FREECAD ASSEMBLY — COMPONENT RECIPES ("roommake")

This assembly document has 24 components, labeled P0..P23 below (a component is one placed body or linked part). 22 of them carry a construction recipe — the FreeCAD feature program that regenerates the part from scratch, quoted from this document or its linked companion documents; the rest are supplied as boundary geometry only. No exploded tour is included for this assembly.
NOTE — this tour is split across 3 documents so each fits a 32k-token context. This is document 1: the component sections continue in the remaining 2 documents, each repeating the header above.
COMPONENT P0 — recipe-attached ("balanceball", a linked part whose construction recipe lives in a companion FreeCAD document of the same project; that document's serialized recipe follows).
Construction recipe (the companion document, serialized — sketch geometry with constraints, then the solid features built on it; lengths are millimeters unless a unit is written):

FCSTD DOCUMENT  (FreeCAD 1.0R39109 (Git))
Label: balanceball
License: All rights reserved
LicenseURL: https://en.wikipedia.org/wiki/All_rights_reserved
objects: Sketcher::SketchObject×4, PartDesign::Body×3, PartDesign::AdditiveSphere×2, PartDesign::Plane×2, App::Part×2, PartDesign::Pad×1, Part::MultiCommon×1, PartDesign::ShapeBinder×1, PartDesign::AdditivePipe×1, Part::MultiFuse×1, Part::FeaturePython×1
note: 29 computed .brp shape members not serialized (recipe doc carries the construction recipe); baked Part::Feature solids carry a one-line shape summary decoded from their .brp

FEATURE [PartDesign::AdditiveSphere] Sphere
  Angle1 = -90
  Angle2 = 90
  Angle3 = 360
  AttacherType = Attacher::AttachEngine3D
  Radius = 275
  Refine = true
  Suppressed = false
FEATURE [Sketcher::SketchObject] Sketch
  ArcFitTolerance = 1e-06
  AttachmentSupport = -> [XZ_Plane]
  ExternalGeometry = -> [Sphere]
  FullyConstrained = false
  MakeInternals = false
  MapMode = 5
  Placement = pos=(0,0,0) rot=(1,0,0;1.5708rad)
  sketch-geometry (131):
    g0: LineSegment StartX=-291.447 StartY=9.66667 StartZ=0 EndX=-291.447 EndY=10.6667 EndZ=0
    g1: LineSegment StartX=-291.447 StartY=10.6667 StartZ=0 EndX=291.447 EndY=10.6667 EndZ=0
    g2: LineSegment StartX=291.447 StartY=10.6667 StartZ=0 EndX=291.447 EndY=9.66667 EndZ=0
    g3: LineSegment StartX=291.447 StartY=9.66667 StartZ=0 EndX=-291.447 EndY=9.66667 EndZ=0
    g4: LineSegment StartX=-280.491 StartY=30 StartZ=0 EndX=-280.491 EndY=31 EndZ=0
    g5: LineSegment StartX=-280.491 StartY=31 StartZ=0 EndX=280.491 EndY=31 EndZ=0
    g6: LineSegment StartX=280.491 StartY=31 StartZ=0 EndX=280.491 EndY=30 EndZ=0
    g7: LineSegment StartX=280.491 StartY=30 StartZ=0 EndX=-280.491 EndY=30 EndZ=0
    g8: LineSegment StartX=282.77 StartY=51.3333 StartZ=0 EndX=282.77 EndY=50.3333 EndZ=0
    g9: LineSegment StartX=282.77 StartY=50.3333 StartZ=0 EndX=-282.77 EndY=50.3333 EndZ=0
    g10: LineSegment StartX=-282.77 StartY=50.3333 StartZ=0 EndX=-282.77 EndY=51.3333 EndZ=0
    g11: LineSegment StartX=-282.77 StartY=51.3333 StartZ=0 EndX=282.77 EndY=51.3333 EndZ=0
    g12: LineSegment StartX=-276.996 StartY=70.6667 StartZ=0 EndX=-276.996 EndY=71.6667 EndZ=0
    g13: LineSegment StartX=-276.996 StartY=71.6667 StartZ=0 EndX=276.996 EndY=71.6667 EndZ=0
    g14: LineSegment StartX=276.996 StartY=71.6667 StartZ=0 EndX=276.996 EndY=70.6667 EndZ=0
    g15: LineSegment StartX=276.996 StartY=70.6667 StartZ=0 EndX=-276.996 EndY=70.6667 EndZ=0
    g16: LineSegment StartX=271.883 StartY=91 StartZ=0 EndX=-271.883 EndY=91 EndZ=0
    g17: LineSegment StartX=-271.883 StartY=91 StartZ=0 EndX=-271.883 EndY=92 EndZ=0
    g18: LineSegment StartX=-271.883 StartY=92 StartZ=0 EndX=271.883 EndY=92 EndZ=0
    g19: LineSegment StartX=271.883 StartY=92 StartZ=0 EndX=271.883 EndY=91 EndZ=0
    g20: LineSegment StartX=-264.412 StartY=112.333 StartZ=0 EndX=264.412 EndY=112.333 EndZ=0
    g21: LineSegment StartX=264.412 StartY=112.333 StartZ=0 EndX=264.412 EndY=111.333 EndZ=0
    g22: LineSegment StartX=264.412 StartY=111.333 StartZ=0 EndX=-264.412 EndY=111.333 EndZ=0
    g23: LineSegment StartX=-264.412 StartY=111.333 StartZ=0 EndX=-264.412 EndY=112.333 EndZ=0
    g24: LineSegment StartX=256.154 StartY=132.667 StartZ=0 EndX=256.154 EndY=131.667 EndZ=0
    g25: LineSegment StartX=256.154 StartY=131.667 StartZ=0 EndX=-256.154 EndY=131.667 EndZ=0
    g26: LineSegment StartX=-256.154 StartY=131.667 StartZ=0 EndX=-256.154 EndY=132.667 EndZ=0
    g27: LineSegment StartX=-256.154 StartY=132.667 StartZ=0 EndX=256.154 EndY=132.667 EndZ=0
    g28: LineSegment StartX=-246.008 StartY=153 StartZ=0 EndX=246.008 EndY=153 EndZ=0
    g29: LineSegment StartX=246.008 StartY=153 StartZ=0 EndX=246.008 EndY=152 EndZ=0
    g30: LineSegment StartX=246.008 StartY=152 StartZ=0 EndX=-246.008 EndY=152 EndZ=0
    g31: LineSegment StartX=-246.008 StartY=152 StartZ=0 EndX=-246.008 EndY=153 EndZ=0
    g32: LineSegment StartX=237.302 StartY=173.333 StartZ=0 EndX=237.302 EndY=172.333 EndZ=0
    g33: LineSegment StartX=237.302 StartY=172.333 StartZ=0 EndX=-237.302 EndY=172.333 EndZ=0
    g34: LineSegment StartX=-237.302 StartY=172.333 StartZ=0 EndX=-237.302 EndY=173.333 EndZ=0
    g35: LineSegment StartX=-237.302 StartY=173.333 StartZ=0 EndX=237.302 EndY=173.333 EndZ=0
    g36: LineSegment StartX=-221.839 StartY=192.667 StartZ=0 EndX=-221.839 EndY=193.667 EndZ=0
    g37: LineSegment StartX=-221.839 StartY=193.667 StartZ=0 EndX=221.839 EndY=193.667 EndZ=0
    g38: LineSegment StartX=221.839 StartY=193.667 StartZ=0 EndX=221.839 EndY=192.667 EndZ=0
    g39: LineSegment StartX=221.839 StartY=192.667 StartZ=0 EndX=-221.839 EndY=192.667 EndZ=0
    g40: LineSegment StartX=212.405 StartY=214 StartZ=0 EndX=212.405 EndY=213 EndZ=0
    g41: LineSegment StartX=212.405 StartY=213 StartZ=0 EndX=-212.405 EndY=213 EndZ=0
    g42: LineSegment StartX=-212.405 StartY=213 StartZ=0 EndX=-212.405 EndY=214 EndZ=0
    g43: LineSegment StartX=-212.405 StartY=214 StartZ=0 EndX=212.405 EndY=214 EndZ=0
    g44: LineSegment StartX=-195.863 StartY=234.333 StartZ=0 EndX=195.863 EndY=234.333 EndZ=0
    g45: LineSegment StartX=195.863 StartY=234.333 StartZ=0 EndX=195.863 EndY=233.333 EndZ=0
    g46: LineSegment StartX=195.863 StartY=233.333 StartZ=0 EndX=-195.863 EndY=233.333 EndZ=0
    g47: LineSegment StartX=-195.863 StartY=233.333 StartZ=0 EndX=-195.863 EndY=234.333 EndZ=0
    g48: LineSegment StartX=184.098 StartY=254.667 StartZ=0 EndX=184.098 EndY=253.667 EndZ=0
    g49: LineSegment StartX=184.098 StartY=253.667 StartZ=0 EndX=-184.098 EndY=253.667 EndZ=0
    g50: LineSegment StartX=-184.098 StartY=253.667 StartZ=0 EndX=-184.098 EndY=254.667 EndZ=0
    g51: LineSegment StartX=-184.098 StartY=254.667 StartZ=0 EndX=184.098 EndY=254.667 EndZ=0
    g52: LineSegment StartX=-283.15 StartY=-10.6667 StartZ=0 EndX=-283.15 EndY=-9.66667 EndZ=0
    g53: LineSegment StartX=-283.15 StartY=-9.66667 StartZ=0 EndX=283.15 EndY=-9.66667 EndZ=0
    g54: LineSegment StartX=283.15 StartY=-9.66667 StartZ=0 EndX=283.15 EndY=-10.6667 EndZ=0
    g55: LineSegment StartX=283.15 StartY=-10.6667 StartZ=0 EndX=-283.15 EndY=-10.6667 EndZ=0
    g56: LineSegment StartX=285.733 StartY=-31 StartZ=0 EndX=-285.733 EndY=-31 EndZ=0
    g57: LineSegment StartX=-285.733 StartY=-31 StartZ=0 EndX=-285.733 EndY=-30 EndZ=0
    g58: LineSegment StartX=-285.733 StartY=-30 StartZ=0 EndX=285.733 EndY=-30 EndZ=0
    g59: LineSegment StartX=285.733 StartY=-30 StartZ=0 EndX=285.733 EndY=-31 EndZ=0
    g60: LineSegment StartX=-283.692 StartY=-51.3333 StartZ=0 EndX=-283.692 EndY=-50.3333 EndZ=0
    g61: LineSegment StartX=-283.692 StartY=-50.3333 StartZ=0 EndX=283.692 EndY=-50.3333 EndZ=0
    g62: LineSegment StartX=283.692 StartY=-50.3333 StartZ=0 EndX=283.692 EndY=-51.3333 EndZ=0
    g63: LineSegment StartX=283.692 StartY=-51.3333 StartZ=0 EndX=-283.692 EndY=-51.3333 EndZ=0
    g64: LineSegment StartX=278.903 StartY=-71.6667 StartZ=0 EndX=-278.903 EndY=-71.6667 EndZ=0
    g65: LineSegment StartX=-278.903 StartY=-71.6667 StartZ=0 EndX=-278.903 EndY=-70.6667 EndZ=0
    g66: LineSegment StartX=-278.903 StartY=-70.6667 StartZ=0 EndX=278.903 EndY=-70.6667 EndZ=0
    g67: LineSegment StartX=278.903 StartY=-70.6667 StartZ=0 EndX=278.903 EndY=-71.6667 EndZ=0
    g68: LineSegment StartX=-269.142 StartY=-92 StartZ=0 EndX=-269.142 EndY=-91 EndZ=0
    g69: LineSegment StartX=-269.142 StartY=-91 StartZ=0 EndX=269.142 EndY=-91 EndZ=0
    g70: LineSegment StartX=269.142 StartY=-91 StartZ=0 EndX=269.142 EndY=-92 EndZ=0
    g71: LineSegment StartX=269.142 StartY=-92 StartZ=0 EndX=-269.142 EndY=-92 EndZ=0
    g72: LineSegment StartX=260.857 StartY=-112.333 StartZ=0 EndX=-260.857 EndY=-112.333 EndZ=0
    g73: LineSegment StartX=-260.857 StartY=-112.333 StartZ=0 EndX=-260.857 EndY=-111.333 EndZ=0
    g74: LineSegment StartX=-260.857 StartY=-111.333 StartZ=0 EndX=260.857 EndY=-111.333 EndZ=0
    g75: LineSegment StartX=260.857 StartY=-111.333 StartZ=0 EndX=260.857 EndY=-112.333 EndZ=0
    g76: LineSegment StartX=-246.128 StartY=-132.667 StartZ=0 EndX=-246.128 EndY=-131.667 EndZ=0
    g77: LineSegment StartX=-246.128 StartY=-131.667 StartZ=0 EndX=246.128 EndY=-131.667 EndZ=0
    g78: LineSegment StartX=246.128 StartY=-131.667 StartZ=0 EndX=246.128 EndY=-132.667 EndZ=0
    g79: LineSegment StartX=246.128 StartY=-132.667 StartZ=0 EndX=-246.128 EndY=-132.667 EndZ=0
    g80: LineSegment StartX=237.57 StartY=-153 StartZ=0 EndX=-237.57 EndY=-153 EndZ=0
    g81: LineSegment StartX=-237.57 StartY=-153 StartZ=0 EndX=-237.57 EndY=-152 EndZ=0
    g82: LineSegment StartX=-237.57 StartY=-152 StartZ=0 EndX=237.57 EndY=-152 EndZ=0
    g83: LineSegment StartX=237.57 StartY=-152 StartZ=0 EndX=237.57 EndY=-153 EndZ=0
    g84: LineSegment StartX=-225.124 StartY=-173.333 StartZ=0 EndX=-225.124 EndY=-172.333 EndZ=0
    g85: LineSegment StartX=-225.124 StartY=-172.333 StartZ=0 EndX=225.124 EndY=-172.333 EndZ=0
    g86: LineSegment StartX=225.124 StartY=-172.333 StartZ=0 EndX=225.124 EndY=-173.333 EndZ=0
    g87: LineSegment StartX=225.124 StartY=-173.333 StartZ=0 EndX=-225.124 EndY=-173.333 EndZ=0
    g88: LineSegment StartX=209.157 StartY=-193.667 StartZ=0 EndX=-209.157 EndY=-193.667 EndZ=0
    g89: LineSegment StartX=-209.157 StartY=-193.667 StartZ=0 EndX=-209.157 EndY=-192.667 EndZ=0
    g90: LineSegment StartX=-209.157 StartY=-192.667 StartZ=0 EndX=209.157 EndY=-192.667 EndZ=0
    g91: LineSegment StartX=209.157 StartY=-192.667 StartZ=0 EndX=209.157 EndY=-193.667 EndZ=0
    g92: LineSegment StartX=-190.627 StartY=-214 StartZ=0 EndX=-190.627 EndY=-213 EndZ=0
    g93: LineSegment StartX=-190.627 StartY=-213 StartZ=0 EndX=190.627 EndY=-213 EndZ=0
    g94: LineSegment StartX=190.627 StartY=-213 StartZ=0 EndX=190.627 EndY=-214 EndZ=0
    g95: LineSegment StartX=190.627 StartY=-214 StartZ=0 EndX=-190.627 EndY=-214 EndZ=0
    g96: LineSegment StartX=-172.023 StartY=-234.333 StartZ=0 EndX=-172.023 EndY=-233.333 EndZ=0
    g97: LineSegment StartX=-172.023 StartY=-233.333 StartZ=0 EndX=172.023 EndY=-233.333 EndZ=0
    g98: LineSegment StartX=172.023 StartY=-233.333 StartZ=0 EndX=172.023 EndY=-234.333 EndZ=0
    g99: LineSegment StartX=172.023 StartY=-234.333 StartZ=0 EndX=-172.023 EndY=-234.333 EndZ=0
    g100: LineSegment StartX=-150.671 StartY=-254.667 StartZ=0 EndX=-150.671 EndY=-253.667 EndZ=0
    g101: LineSegment StartX=-150.671 StartY=-253.667 StartZ=0 EndX=150.671 EndY=-253.667 EndZ=0
    g102: LineSegment StartX=150.671 StartY=-253.667 StartZ=0 EndX=150.671 EndY=-254.667 EndZ=0
    g103: LineSegment StartX=150.671 StartY=-254.667 StartZ=0 EndX=-150.671 EndY=-254.667 EndZ=0
    g104: LineSegment [constr] StartX=8.42e-14 StartY=275 StartZ=0 EndX=8.42e-14 EndY=253.667 EndZ=0
    g105: LineSegment [constr] StartX=7.37e-14 StartY=254.667 StartZ=0 EndX=7.37e-14 EndY=233.333 EndZ=0
    g106: LineSegment [constr] StartX=6.83e-14 StartY=234.333 StartZ=0 EndX=6.83e-14 EndY=213 EndZ=0
    g107: LineSegment [constr] StartX=9.01e-14 StartY=214 StartZ=0 EndX=9.01e-14 EndY=192.667 EndZ=0
    g108: LineSegment [constr] StartX=7.41e-14 StartY=193.667 StartZ=0 EndX=7.41e-14 EndY=172.333 EndZ=0
    g109: LineSegment [constr] StartX=8.64e-14 StartY=173.333 StartZ=0 EndX=8.64e-14 EndY=152 EndZ=0
    g110: LineSegment [constr] StartX=8.72e-14 StartY=153 StartZ=0 EndX=8.72e-14 EndY=131.667 EndZ=0
    g111: LineSegment [constr] StartX=1.192e-13 StartY=132.667 StartZ=0 EndX=1.192e-13 EndY=111.333 EndZ=0
    g112: LineSegment [constr] StartX=1.25e-13 StartY=112.333 StartZ=0 EndX=1.25e-13 EndY=91 EndZ=0
    g113: LineSegment [constr] StartX=1.363e-13 StartY=92 StartZ=0 EndX=1.363e-13 EndY=70.6667 EndZ=0
    g114: LineSegment [constr] StartX=1.131e-13 StartY=71.6667 StartZ=0 EndX=1.131e-13 EndY=50.3333 EndZ=0
    g115: LineSegment [constr] StartX=8.7e-14 StartY=51.3333 StartZ=0 EndX=8.7e-14 EndY=30 EndZ=0
    g116: LineSegment [constr] StartX=1.326e-13 StartY=31 StartZ=0 EndX=1.326e-13 EndY=9.66667 EndZ=0
    g117: LineSegment [constr] StartX=9.7e-14 StartY=10.6667 StartZ=0 EndX=9.7e-14 EndY=-10.6667 EndZ=0
    g118: LineSegment [constr] StartX=1.219e-13 StartY=-9.66667 StartZ=0 EndX=1.219e-13 EndY=-31 EndZ=0
    g119: LineSegment [constr] StartX=8.3e-14 StartY=-30 StartZ=0 EndX=8.3e-14 EndY=-51.3333 EndZ=0
    g120: LineSegment [constr] StartX=9.47e-14 StartY=-50.3333 StartZ=0 EndX=9.47e-14 EndY=-71.6667 EndZ=0
    g121: LineSegment [constr] StartX=1.138e-13 StartY=-70.6667 StartZ=0 EndX=1.138e-13 EndY=-92 EndZ=0
    g122: LineSegment [constr] StartX=1.058e-13 StartY=-91 StartZ=0 EndX=1.058e-13 EndY=-112.333 EndZ=0
    g123: LineSegment [constr] StartX=1.327e-13 StartY=-111.333 StartZ=0 EndX=1.327e-13 EndY=-132.667 EndZ=0
    g124: LineSegment [constr] StartX=1.275e-13 StartY=-131.667 StartZ=0 EndX=1.275e-13 EndY=-153 EndZ=0
    g125: LineSegment [constr] StartX=1.325e-13 StartY=-152 StartZ=0 EndX=1.325e-13 EndY=-173.333 EndZ=0
    g126: LineSegment [constr] StartX=1.362e-13 StartY=-172.333 StartZ=0 EndX=1.362e-13 EndY=-193.667 EndZ=0
    g127: LineSegment [constr] StartX=1.246e-13 StartY=-192.667 StartZ=0 EndX=1.246e-13 EndY=-214 EndZ=0
    g128: LineSegment [constr] StartX=1.449e-13 StartY=-213 StartZ=0 EndX=1.449e-13 EndY=-234.333 EndZ=0
    g129: LineSegment [constr] StartX=1.405e-13 StartY=-233.333 StartZ=0 EndX=1.405e-13 EndY=-254.667 EndZ=0
    g130: LineSegment [constr] StartX=1.48e-13 StartY=-253.667 StartZ=0 EndX=-5.05e-14 EndY=-275 EndZ=0
  constraints (340):
    c: Coincident(g0,g1)
    c: Coincident(g1,g2)
    c: Coincident(g2,g3)
    c: Coincident(g3,g0)
    c: Vertical(g0)
    c: Vertical(g2)
    c: Horizontal(g1)
    c: Horizontal(g3)
    c: Coincident(g4,g5)
    c: Coincident(g5,g6)
    c: Coincident(g6,g7)
    c: Coincident(g7,g4)
    c: Vertical(g4)
    c: Vertical(g6)
    c: Horizontal(g5)
    c: Horizontal(g7)
    c: Coincident(g8,g9)
    c: Coincident(g9,g10)
    c: Coincident(g10,g11)
    c: Coincident(g11,g8)
    c: Vertical(g8)
    c: Vertical(g10)
    c: Horizontal(g9)
    c: Horizontal(g11)
    c: Coincident(g12,g13)
    c: Coincident(g13,g14)
    c: Coincident(g14,g15)
    c: Coincident(g15,g12)
    c: Vertical(g12)
    c: Vertical(g14)
    c: Horizontal(g13)
    c: Horizontal(g15)
    c: Coincident(g16,g17)
    c: Coincident(g17,g18)
    c: Coincident(g18,g19)
    c: Coincident(g19,g16)
    c: Horizontal(g16)
    c: Horizontal(g18)
    c: Vertical(g17)
    c: Vertical(g19)
    c: Coincident(g20,g21)
    c: Coincident(g21,g22)
    c: Coincident(g22,g23)
    c: Coincident(g23,g20)
    c: Horizontal(g20)
    c: Horizontal(g22)
    c: Vertical(g21)
    c: Vertical(g23)
    c: Coincident(g24,g25)
    c: Coincident(g25,g26)
    c: Coincident(g26,g27)
    c: Coincident(g27,g24)
    c: Vertical(g24)
    c: Vertical(g26)
    c: Horizontal(g25)
    c: Horizontal(g27)
    c: Coincident(g28,g29)
    c: Coincident(g29,g30)
    c: Coincident(g30,g31)
    c: Coincident(g31,g28)
    c: Horizontal(g28)
    c: Horizontal(g30)
    c: Vertical(g29)
    c: Vertical(g31)
    c: Coincident(g32,g33)
    c: Coincident(g33,g34)
    c: Coincident(g34,g35)
    c: Coincident(g35,g32)
    c: Vertical(g32)
    c: Vertical(g34)
    c: Horizontal(g33)
    c: Horizontal(g35)
    c: Coincident(g36,g37)
    c: Coincident(g37,g38)
    c: Coincident(g38,g39)
    c: Coincident(g39,g36)
    c: Vertical(g36)
    c: Vertical(g38)
    c: Horizontal(g37)
    c: Horizontal(g39)
    c: Coincident(g40,g41)
    c: Coincident(g41,g42)
    c: Coincident(g42,g43)
    c: Coincident(g43,g40)
    c: Vertical(g40)
    c: Vertical(g42)
    c: Horizontal(g41)
    c: Horizontal(g43)
    c: Coincident(g44,g45)
    c: Coincident(g45,g46)
    c: Coincident(g46,g47)
    c: Coincident(g47,g44)
    c: Horizontal(g44)
    c: Horizontal(g46)
    c: Vertical(g45)
    c: Vertical(g47)
    c: Coincident(g48,g49)
    c: Coincident(g49,g50)
    c: Coincident(g50,g51)
    c: Coincident(g51,g48)
    c: Vertical(g48)
    c: Vertical(g50)
    c: Horizontal(g49)
    c: Horizontal(g51)
    c: Coincident(g52,g53)
    c: Coincident(g53,g54)
    c: Coincident(g54,g55)
    c: Coincident(g55,g52)
    c: Vertical(g52)
    c: Vertical(g54)
    c: Horizontal(g53)
    c: Horizontal(g55)
    c: Coincident(g56,g57)
    c: Coincident(g57,g58)
    c: Coincident(g58,g59)
    c: Coincident(g59,g56)
    c: Horizontal(g56)
    c: Horizontal(g58)
    c: Vertical(g57)
    c: Vertical(g59)
    c: Coincident(g60,g61)
    c: Coincident(g61,g62)
    c: Coincident(g62,g63)
    c: Coincident(g63,g60)
    c: Vertical(g60)
    c: Vertical(g62)
    c: Horizontal(g61)
    c: Horizontal(g63)
    c: Coincident(g64,g65)
    c: Coincident(g65,g66)
    c: Coincident(g66,g67)
    c: Coincident(g67,g64)
    c: Horizontal(g64)
    c: Horizontal(g66)
    c: Vertical(g65)
    c: Vertical(g67)
    c: Coincident(g68,g69)
    c: Coincident(g69,g70)
    c: Coincident(g70,g71)
    c: Coincident(g71,g68)
    c: Vertical(g68)
    c: Vertical(g70)
    c: Horizontal(g69)
    c: Horizontal(g71)
    c: Coincident(g72,g73)
    c: Coincident(g73,g74)
    c: Coincident(g74,g75)
    c: Coincident(g75,g72)
    c: Horizontal(g72)
    c: Horizontal(g74)
    c: Vertical(g73)
    c: Vertical(g75)
    c: Coincident(g76,g77)
    c: Coincident(g77,g78)
    c: Coincident(g78,g79)
    c: Coincident(g79,g76)
    c: Vertical(g76)
    c: Vertical(g78)
    c: Horizontal(g77)
    c: Horizontal(g79)
    c: Coincident(g80,g81)
    c: Coincident(g81,g82)
    c: Coincident(g82,g83)
    c: Coincident(g83,g80)
    c: Horizontal(g80)
    c: Horizontal(g82)
    c: Vertical(g81)
    c: Vertical(g83)
    c: Coincident(g84,g85)
    c: Coincident(g85,g86)
    c: Coincident(g86,g87)
    c: Coincident(g87,g84)
    c: Vertical(g84)
    c: Vertical(g86)
    c: Horizontal(g85)
    c: Horizontal(g87)
    c: Coincident(g88,g89)
    c: Coincident(g89,g90)
    c: Coincident(g90,g91)
    c: Coincident(g91,g88)
    c: Horizontal(g88)
    c: Horizontal(g90)
    c: Vertical(g89)
    c: Vertical(g91)
    c: Coincident(g92,g93)
    c: Coincident(g93,g94)
    c: Coincident(g94,g95)
    c: Coincident(g95,g92)
    c: Vertical(g92)
    c: Vertical(g94)
    c: Horizontal(g93)
    c: Horizontal(g95)
    c: Coincident(g96,g97)
    c: Coincident(g97,g98)
    c: Coincident(g98,g99)
    c: Coincident(g99,g96)
    c: Vertical(g96)
    c: Vertical(g98)
    c: Horizontal(g97)
    c: Horizontal(g99)
    c: Coincident(g100,g101)
    c: Coincident(g101,g102)
    c: Coincident(g102,g103)
    c: Coincident(g103,g100)
    c: Vertical(g100)
    c: Vertical(g102)
    c: Horizontal(g101)
    c: Horizontal(g103)
    c: Equal(g50,g47)
    c: Equal(g47,g42)
    c: Equal(g42,g36)
    c: Equal(g36,g34)
    c: Equal(g34,g31)
    c: Equal(g31,g26)
    c: Equal(g26,g23)
    c: Equal(g23,g17)
    c: Equal(g17,g12)
    c: Equal(g12,g10)
    c: Equal(g10,g4)
    c: Equal(g4,g0)
    c: Equal(g0,g52)
    c: Equal(g52,g57)
    c: Equal(g57,g60)
    c: Equal(g60,g65)
    c: Equal(g65,g68)
    c: Equal(g68,g73)
    c: Equal(g73,g76)
    c: Equal(g76,g81)
    c: Equal(g81,g84)
    c: Equal(g84,g89)
    c: Equal(g89,g92)
    c: Equal(g92,g96)
    c: Equal(g96,g100)
    c: Coincident(g104,g-3)
    c: Symmetric(g49,g49,g104)
    c: Symmetric(g51,g51,g105)
    c: Symmetric(g46,g46,g105)
    c: Symmetric(g44,g44,g106)
    c: Symmetric(g41,g41,g106)
    c: Symmetric(g43,g43,g107)
    c: Symmetric(g39,g39,g107)
    c: Symmetric(g37,g37,g108)
    c: Symmetric(g33,g33,g108)
    c: Vertical(g108)
    c: Symmetric(g35,g35,g109)
    c: Symmetric(g30,g30,g109)
    c: Symmetric(g28,g28,g110)
    c: Symmetric(g25,g25,g110)
    c: Symmetric(g27,g27,g111)
    c: Symmetric(g22,g22,g111)
    c: Vertical(g111)
    c: Symmetric(g20,g20,g112)
    c: Symmetric(g16,g16,g112)
    c: Vertical(g112)
    c: Symmetric(g18,g18,g113)
    c: Symmetric(g15,g15,g113)
    c: Symmetric(g13,g13,g114)
    c: Symmetric(g9,g9,g114)
    c: Symmetric(g11,g11,g115)
    c: Symmetric(g7,g7,g115)
    c: Vertical(g115)
    c: Symmetric(g5,g5,g116)
    c: Symmetric(g3,g3,g116)
    c: Symmetric(g1,g1,g117)
    c: Symmetric(g55,g55,g117)
    c: Symmetric(g53,g53,g118)
    c: Symmetric(g56,g56,g118)
    c: Symmetric(g58,g58,g119)
    c: Symmetric(g63,g63,g119)
    c: Symmetric(g61,g61,g120)
    c: Symmetric(g64,g64,g120)
    c: Symmetric(g66,g66,g121)
    c: Symmetric(g71,g71,g121)
    c: Symmetric(g69,g69,g122)
    c: Symmetric(g72,g72,g122)
    c: Vertical(g122)
    c: Symmetric(g74,g74,g123)
    c: Symmetric(g79,g79,g123)
    c: Symmetric(g77,g77,g124)
    c: Symmetric(g80,g80,g124)
    c: Symmetric(g82,g82,g125)
    c: Symmetric(g87,g87,g125)
    c: Symmetric(g85,g85,g126)
    c: Symmetric(g88,g88,g126)
    c: Symmetric(g90,g90,g127)
    c: Symmetric(g95,g95,g127)
    c: Symmetric(g93,g93,g128)
    c: Symmetric(g99,g99,g128)
    c: Symmetric(g97,g97,g129)
    c: Symmetric(g103,g103,g129)
    c: Symmetric(g101,g101,g130)
    c: Coincident(g130,g-3)
    c: Equal(g104,g105)
    c: Equal(g105,g106)
    c: Equal(g106,g107)
    c: Equal(g107,g108)
    c: Equal(g108,g109)
    c: Equal(g109,g110)
    c: Equal(g110,g111)
    c: Equal(g111,g112)
    c: Equal(g112,g113)
    c: Equal(g113,g114)
    c: Equal(g114,g115)
    c: Equal(g115,g116)
    c: Equal(g116,g117)
    c: Equal(g117,g118)
    c: Equal(g118,g119)
    c: Equal(g119,g120)
    c: Equal(g120,g121)
    c: Equal(g121,g122)
    c: Equal(g122,g123)
    c: Equal(g123,g124)
    c: Equal(g124,g125)
    c: Equal(g125,g126)
    c: Equal(g126,g127)
    c: Equal(g127,g128)
    c: Equal(g128,g129)
    c: Equal(g129,g130)
    c: Vertical(g104)
    c: Vertical(g105)
    c: Vertical(g106)
    c: Vertical(g107)
    c: Vertical(g109)
    c: Vertical(g110)
    c: Vertical(g113)
    c: Vertical(g114)
    c: Vertical(g116)
    c: Vertical(g117)
    c: Vertical(g118)
    c: Vertical(g119)
    c: Vertical(g120)
    c: Vertical(g121)
    c: Vertical(g123)
    c: Vertical(g124)
    c: Vertical(g125)
    c: Vertical(g126)
    c: Vertical(g127)
    c: Vertical(g128)
    c: Vertical(g129)
    c: DistanceY(g50,g50) = 1
FEATURE [PartDesign::Pad] Pad
  BaseFeature = -> Sphere
  Direction = (0,-1,2e-16)
  Length = 560
  Length2 = 10
  Midplane = true
  Profile = -> Sketch
  ReferenceAxis = -> Sketch [N_Axis]
  Refine = true
  Suppressed = false
  Type = 0
FEATURE [PartDesign::Body] Body
  AllowCompound = false
  Group = -> [Sphere,Sketch,Pad]
  Origin = -> Origin
  Tip = -> Pad
FEATURE [PartDesign::AdditiveSphere] Sphere001
  Angle1 = -90
  Angle2 = 90
  Angle3 = 360
  AttacherType = Attacher::AttachEngine3D
  Radius = 275.5
  Refine = true
  Suppressed = false
FEATURE [PartDesign::Body] Body001
  AllowCompound = false
  Group = -> [Sphere001]
  Origin = -> Origin001
  Tip = -> Sphere001
FEATURE [Part::MultiCommon] Common
  Refine = true
  Shapes = -> [Body,Body001]
FEATURE [PartDesign::ShapeBinder] CopyCommon
  TraceSupport = false
FEATURE [Sketcher::SketchObject] Sketch001
  ArcFitTolerance = 1e-06
  AttachmentSupport = -> [XZ_Plane002]
  ExternalGeometry = -> [CopyCommon]
  FullyConstrained = false
  MakeInternals = false
  MapMode = 5
  Placement = pos=(0,0,0) rot=(1,0,0;1.5708rad)
  sketch-geometry (2):
    g0: Circle CenterX=-157.732 CenterY=-255.772 CenterZ=0 NormalX=0 NormalY=0 NormalZ=1 AngleXU=0 Radius=25
    g1: LineSegment StartX=-144.873 StartY=-234.333 StartZ=0 EndX=-157.732 EndY=-255.772 EndZ=0
  constraints (4):
    c: PointOnObject(g-3,g0)
    c: Radius(g0) = 25
    c: Coincident(g1,g-3)
    c: Coincident(g1,g0)
FEATURE [PartDesign::Plane] DatumPlane
  AttachmentSupport = -> [Sketch001]
  Length = 438.471
  MapMode = 1
  Placement = pos=(-157.732,-5.68e-14,-255.772) rot=(0,0,1;0rad)
  ResizeMode = 0
  Width = 438.506
FEATURE [Sketcher::SketchObject] Sketch002
  ArcFitTolerance = 1e-06
  AttachmentSupport = -> [DatumPlane]
  ExternalGeometry = -> [CopyCommon]
  FullyConstrained = true
  MakeInternals = false
  MapMode = 5
  Placement = pos=(-157.732,-5.68e-14,-255.772) rot=(0,0,1;0rad)
  sketch-geometry (1):
    g0: Circle CenterX=157.732 CenterY=4.8e-15 CenterZ=0 NormalX=0 NormalY=0 NormalZ=1 AngleXU=0 Radius=157.732
  constraints (2):
    c: Coincident(g0,g-3)
    c: PointOnObject(g-1,g0)
FEATURE [PartDesign::Plane] DatumPlane001
  AttachmentSupport = -> [Sketch001]
  Length = 372.613
  MapMode = 11
  Placement = pos=(-157.732,-5.68e-14,-255.772) rot=(0.57735,-0.57735,0.57735;2.0944rad)
  ResizeMode = 0
  Width = 432.239
FEATURE [Sketcher::SketchObject] Sketch003
  ArcFitTolerance = 1e-06
  AttachmentSupport = -> [DatumPlane001]
  ExternalGeometry = -> [Sketch001]
  FullyConstrained = false
  MakeInternals = false
  MapMode = 5
  Placement = pos=(-157.732,-5.68e-14,-255.772) rot=(0.57735,-0.57735,0.57735;2.0944rad)
  sketch-geometry (1):
    g0: Circle CenterX=0 CenterY=0 CenterZ=0 NormalX=0 NormalY=0 NormalZ=1 AngleXU=0 Radius=25
  constraints (1):
    c: Coincident(g0,g-1)
FEATURE [PartDesign::AdditivePipe] AdditivePipe
  AuxilleryCurvelinear = true
  AuxillerySpineTangent = false
  Binormal = (0,0,0)
  Mode = 0
  Placement = pos=(-157.732,-5.68e-14,-255.772) rot=(0.57735,-0.57735,0.57735;2.0944rad)
  Profile = -> Sketch003
  Refine = true
  Spine = -> Sketch002
  SpineTangent = false
  Suppressed = false
  Transformation = 0
  Transition = 0
FEATURE [PartDesign::Body] Body002
  AllowCompound = false
  Group = -> [CopyCommon,Sketch001,DatumPlane,Sketch002,DatumPlane001,Sketch003,AdditivePipe]
  Origin = -> Origin002
  Tip = -> AdditivePipe
FEATURE [Part::MultiFuse] Fusion
  Placement = pos=(0,0,280) rot=(0,0,1;0rad)
  Refine = true
  Shapes = -> [Common,Body002]
FEATURE [App::Part] Part  label="balanceball1"
  Group = -> [Body,Body001,Common,Body002,Fusion]
  Origin = -> Origin003
  Placement = pos=(0,0,280) rot=(0,0,1;0rad)
FEATURE [Part::FeaturePython] Clone  label="balanceball_clone"  # Draft clone (typed FeaturePython)
  AttacherType = Attacher::AttachEngine3D
  Fuse = false
  Objects = -> [Part]
  Scale = (1,1,1)
FEATURE [App::Part] Part001  label="balanceball"
  Group = -> [Clone]
  Origin = -> Origin004
COMPONENT P1 — recipe-attached ("clock", a linked part whose construction recipe lives in a companion FreeCAD document of the same project; that document's serialized recipe follows).
Construction recipe (the companion document, serialized — sketch geometry with constraints, then the solid features built on it; lengths are millimeters unless a unit is written):

FCSTD DOCUMENT  (FreeCAD 1.0R39109 (Git))
Label: clock
License: All rights reserved
LicenseURL: https://en.wikipedia.org/wiki/All_rights_reserved
objects: Part::FeaturePython×13, App::Part×13, Sketcher::SketchObject×6, PartDesign::Body×6, PartDesign::ShapeBinder×5, PartDesign::Pad×5, PartDesign::Revolution×1
note: 53 computed .brp shape members not serialized (recipe doc carries the construction recipe); baked Part::Feature solids carry a one-line shape summary decoded from their .brp

FEATURE [Sketcher::SketchObject] Sketch
  ArcFitTolerance = 1e-06
  AttachmentSupport = -> [XZ_Plane]
  FullyConstrained = true
  MakeInternals = false
  MapMode = 5
  Placement = pos=(0,0,0) rot=(1,0,0;1.5708rad)
  sketch-geometry (12):
    g0: LineSegment StartX=0 StartY=0 StartZ=0 EndX=150 EndY=0 EndZ=0
    g1: LineSegment StartX=150 StartY=0 StartZ=0 EndX=150 EndY=55 EndZ=0
    g2: LineSegment StartX=150 StartY=55 StartZ=0 EndX=135 EndY=55 EndZ=0
    g3: LineSegment StartX=135 StartY=55 StartZ=0 EndX=135 EndY=50 EndZ=0
    g4: LineSegment StartX=135 StartY=50 StartZ=0 EndX=140 EndY=50 EndZ=0
    g5: LineSegment StartX=140 StartY=50 StartZ=0 EndX=140 EndY=48 EndZ=0
    g6: LineSegment StartX=140 StartY=48 StartZ=0 EndX=135 EndY=48 EndZ=0
    g7: LineSegment StartX=135 StartY=48 StartZ=0 EndX=135 EndY=25 EndZ=0
    g8: LineSegment StartX=135 StartY=25 StartZ=0 EndX=2.5 EndY=25 EndZ=0
    g9: LineSegment StartX=2.5 StartY=25 StartZ=0 EndX=2.5 EndY=28 EndZ=0
    g10: LineSegment StartX=2.5 StartY=28 StartZ=0 EndX=0 EndY=28 EndZ=0
    g11: LineSegment StartX=0 StartY=28 StartZ=0 EndX=0 EndY=0 EndZ=0
  constraints (35):
    c: Coincident(g-1,g0)
    c: PointOnObject(g0,g-1)
    c: Coincident(g0,g1)
    c: Vertical(g1)
    c: Coincident(g1,g2)
    c: Horizontal(g2)
    c: Coincident(g2,g3)
    c: Vertical(g3)
    c: Coincident(g3,g4)
    c: Horizontal(g4)
    c: Coincident(g4,g5)
    c: Vertical(g5)
    c: Coincident(g5,g6)
    c: Horizontal(g6)
    c: Coincident(g6,g7)
    c: Vertical(g7)
    c: Coincident(g7,g8)
    c: Horizontal(g8)
    c: Coincident(g8,g9)
    c: Vertical(g9)
    c: Coincident(g9,g10)
    c: PointOnObject(g10,g-2)
    c: Horizontal(g10)
    c: Coincident(g10,g11)
    c: Coincident(g11,g0)
    c: DistanceX(g0,g0) = 150
    c: DistanceY(g1,g1) = 55
    c: DistanceX(g2,g2) = 15
    c: DistanceY(g3,g3) = 5
    c: DistanceX(g4,g4) = 5
    c: Equal(g4,g6)
    c: DistanceY(g5,g5) = 2
    c: DistanceY(g7,g2) = 30
    c: DistanceY(g9,g9) = 3
    c: DistanceX(g10,g10) = 2.5
FEATURE [PartDesign::Revolution] Revolution
  Angle = 360
  Angle2 = 60
  Axis = (0,2e-16,1)
  Base = (0,0,0)
  Placement = pos=(0,0,0) rot=(1,0,0;1.5708rad)
  Profile = -> Sketch
  ReferenceAxis = -> Sketch [V_Axis]
  Refine = true
  Reversed = true
  Suppressed = false
  Type = 0
FEATURE [PartDesign::Body] Body
  AllowCompound = false
  Group = -> [Sketch,Revolution]
  Origin = -> Origin
  Tip = -> Revolution
FEATURE [PartDesign::ShapeBinder] CopyRevolution
  Placement = pos=(0,0,0) rot=(1,0,0;1.5708rad)
  TraceSupport = false
FEATURE [Sketcher::SketchObject] Sketch001
  ArcFitTolerance = 1e-06
  AttachmentSupport = -> [CopyRevolution]
  FullyConstrained = true
  MakeInternals = false
  MapMode = 5
  Placement = pos=(0,1.1e-14,25) rot=(0,0,1;3.14159rad)
  sketch-geometry (5):
    g0: Circle CenterX=0 CenterY=6e-16 CenterZ=0 NormalX=0 NormalY=0 NormalZ=1 AngleXU=0 Radius=2.5
    g1: ArcOfCircle CenterX=0 CenterY=6e-16 CenterZ=0 NormalX=0 NormalY=0 NormalZ=1 AngleXU=0 Radius=5 StartAngle=1e-16 EndAngle=3.14159
    g2: LineSegment StartX=5 StartY=1.2e-15 StartZ=0 EndX=5 EndY=-100 EndZ=0
    g3: LineSegment StartX=5 StartY=-100 StartZ=0 EndX=-5 EndY=-100 EndZ=0
    g4: LineSegment StartX=-5 StartY=-100 StartZ=0 EndX=-5 EndY=0 EndZ=0
  constraints (13):
    c: Coincident(g1,g0)
    c: Radius(g0) = 2.5
    c: PointOnObject(g0,g-2)
    c: Vertical(g2)
    c: Coincident(g2,g3)
    c: Horizontal(g3)
    c: Coincident(g3,g4)
    c: Vertical(g4)
    c: PointOnObject(g4,g-1)
    c: Tangent(g1,g4) = 1.5708
    c: Tangent(g1,g2) = 1.5708
    c: DistanceX(g3,g3) = 10
    c: DistanceY(g4,g4) = 100
FEATURE [PartDesign::Pad] Pad
  Direction = (0,0,1)
  Length = 1
  Length2 = 10
  Placement = pos=(0,0,0) rot=(1,0,0;1.5708rad)
  Profile = -> Sketch001
  ReferenceAxis = -> Sketch001 [N_Axis]
  Refine = true
  Suppressed = false
  Type = 0
FEATURE [PartDesign::Body] Body001
  AllowCompound = false
  Group = -> [CopyRevolution,Sketch001,Pad]
  Origin = -> Origin001
  Tip = -> Pad
FEATURE [PartDesign::ShapeBinder] CopyRevolution001
  Placement = pos=(0,0,0) rot=(1,0,0;1.5708rad)
  TraceSupport = false
FEATURE [Sketcher::SketchObject] Sketch002
  ArcFitTolerance = 1e-06
  AttachmentSupport = -> [CopyRevolution001]
  FullyConstrained = true
  MakeInternals = false
  MapMode = 5
  Placement = pos=(0,1.1e-14,25) rot=(0,0,1;3.14159rad)
  sketch-geometry (5):
    g0: Circle CenterX=0 CenterY=0 CenterZ=0 NormalX=0 NormalY=0 NormalZ=1 AngleXU=0 Radius=2.5
    g1: ArcOfCircle CenterX=0 CenterY=0 CenterZ=0 NormalX=0 NormalY=0 NormalZ=1 AngleXU=0 Radius=5 StartAngle=0 EndAngle=3.14159
    g2: LineSegment StartX=5 StartY=0 StartZ=0 EndX=5 EndY=-65 EndZ=0
    g3: LineSegment StartX=5 StartY=-65 StartZ=0 EndX=-5 EndY=-65 EndZ=0
    g4: LineSegment StartX=-5 StartY=-65 StartZ=0 EndX=-5 EndY=0 EndZ=0
  constraints (12):
    c: Coincident(g1,g0)
    c: Radius(g0) = 2.5
    c: Coincident(g0,g-1)
    c: PointOnObject(g2,g-1)
    c: Coincident(g2,g3)
    c: Horizontal(g3)
    c: Coincident(g3,g4)
    c: PointOnObject(g4,g-1)
    c: Tangent(g1,g4) = 1.5708
    c: Tangent(g1,g2) = 1.5708
    c: DistanceX(g3,g3) = 10
    c: DistanceY(g4,g4) = 65
FEATURE [PartDesign::Pad] Pad001
  Direction = (0,0,1)
  Length = 1
  Length2 = 10
  Placement = pos=(0,0,0) rot=(1,0,0;1.5708rad)
  Profile = -> Sketch002
  ReferenceAxis = -> Sketch002 [N_Axis]
  Refine = true
  Suppressed = false
  Type = 0
FEATURE [PartDesign::Body] Body002
  AllowCompound = false
  Group = -> [CopyRevolution001,Sketch002,Pad001]
  Origin = -> Origin002
  Placement = pos=(0,0,1) rot=(0,0,1;1.0472rad)
  Tip = -> Pad001
FEATURE [PartDesign::ShapeBinder] CopyRevolution002
  Placement = pos=(0,0,0) rot=(1,0,0;1.5708rad)
  TraceSupport = false
FEATURE [Sketcher::SketchObject] Sketch003
  ArcFitTolerance = 1e-06
  AttachmentSupport = -> [CopyRevolution002]
  FullyConstrained = false
  MakeInternals = false
  MapMode = 5
  Placement = pos=(0,1.1e-14,25) rot=(0,0,1;3.14159rad)
  sketch-geometry (6):
    g0: Circle CenterX=0 CenterY=0 CenterZ=0 NormalX=0 NormalY=0 NormalZ=1 AngleXU=0 Radius=2.5
    g1: ArcOfCircle CenterX=0 CenterY=0 CenterZ=0 NormalX=0 NormalY=0 NormalZ=1 AngleXU=0 Radius=5 StartAngle=0.986756 EndAngle=6.86723
    g2: LineSegment StartX=4.17121 StartY=2.75699 StartZ=0 EndX=88.2635 EndY=86.8493 EndZ=0
    g3: LineSegment StartX=88.2635 StartY=86.8493 StartZ=0 EndX=86.8493 EndY=88.2635 EndZ=0
    g4: LineSegment StartX=2.75699 StartY=4.17121 StartZ=0 EndX=86.8493 EndY=88.2635 EndZ=0
    g5: LineSegment [constr] StartX=0 StartY=0 StartZ=0 EndX=87.5564 EndY=87.5564 EndZ=0
  constraints (14):
    c: Coincident(g0,g-1)
    c: Coincident(g0,g1)
    c: Radius(g0) = 2.5
    c: Coincident(g3,g2)
    c: Coincident(g4,g3)
    c: Coincident(g5,g0)
    c: Symmetric(g3,g3,g5)
    c: Angle(g-1,g5) = 0.785398
    c: Perpendicular(g3,g4)
    c: Perpendicular(g2,g3)
    c: Distance(g3) = 2
    c: Coincident(g1,g2)
    c: Coincident(g1,g4)
    c: Radius(g1) = 5
FEATURE [PartDesign::Pad] Pad002
  Direction = (0,0,1)
  Length = 0.5
  Length2 = 10
  Placement = pos=(0,0,0) rot=(1,0,0;1.5708rad)
  Profile = -> Sketch003
  ReferenceAxis = -> Sketch003 [N_Axis]
  Refine = true
  Suppressed = false
  Type = 0
FEATURE [PartDesign::Body] Body003
  AllowCompound = false
  Group = -> [CopyRevolution002,Sketch003,Pad002]
  Origin = -> Origin003
  Placement = pos=(0,0,2) rot=(0,0,1;0rad)
  Tip = -> Pad002
FEATURE [PartDesign::ShapeBinder] CopyRevolution003
  Placement = pos=(0,0,0) rot=(1,0,0;1.5708rad)
  TraceSupport = false
FEATURE [Sketcher::SketchObject] Sketch004
  ArcFitTolerance = 1e-06
  AttachmentSupport = -> [CopyRevolution003]
  FullyConstrained = true
  MakeInternals = false
  MapMode = 5
  Placement = pos=(0,1.1e-14,25) rot=(0,0,1;3.14159rad)
  sketch-geometry (4):
    g0: LineSegment StartX=-2.5 StartY=-110 StartZ=0 EndX=-2.5 EndY=-130 EndZ=0
    g1: LineSegment StartX=-2.5 StartY=-130 StartZ=0 EndX=2.5 EndY=-130 EndZ=0
    g2: LineSegment StartX=2.5 StartY=-130 StartZ=0 EndX=2.5 EndY=-110 EndZ=0
    g3: LineSegment StartX=2.5 StartY=-110 StartZ=0 EndX=-2.5 EndY=-110 EndZ=0
  constraints (11):
    c: Coincident(g0,g1)
    c: Coincident(g1,g2)
    c: Coincident(g2,g3)
    c: Coincident(g3,g0)
    c: Vertical(g0)
    c: Vertical(g2)
    c: Horizontal(g1)
    c: DistanceY(g0,g0) = 20
    c: DistanceX(g3,g3) = 5
    c: Symmetric(g0,g2,g-2)
    c: DistanceY(g0) = -110
FEATURE [PartDesign::Pad] Pad003
  Direction = (0,0,1)
  Length = 1
  Length2 = 10
  Placement = pos=(0,0,0) rot=(1,0,0;1.5708rad)
  Profile = -> Sketch004
  ReferenceAxis = -> Sketch004 [N_Axis]
  Refine = true
  Suppressed = false
  Type = 0
FEATURE [PartDesign::Body] Body004
  AllowCompound = false
  Group = -> [CopyRevolution003,Sketch004,Pad003]
  Origin = -> Origin004
  Tip = -> Pad003
FEATURE [Part::FeaturePython] Array  # Draft array (typed FeaturePython)
  AlwaysSyncPlacement = false
  Angle = 360
  ArrayType = 1
  Axis = (0,0,1)
  Base = -> Body004
  Center = (0,0,0)
  Count = 12
  ExpandArray = false
  Fuse = false
  IntervalAxis = (0,0,0)
  IntervalX = (100,0,0)
  IntervalY = (0,100,0)
  IntervalZ = (0,0,100)
  NumberCircles = 3
  NumberPolar = 12
  NumberX = 2
  NumberY = 2
  NumberZ = 1
  PlacementList = 12 placements: [(0,0,0),(0,0,0),(0,0,0),(0,0,0),(0,0,0),(0,0,0),(0,0,0),(0,0,0),(0,0,0),(0,0,0),(0,0,0),(0,0,0)]
  RadialDistance = 50
  ScaleList = (12) [(1,1,1),(1,1,1),(1,1,1),(1,1,1),(1,1,1),(1,1,1),(1,1,1),(1,1,1),(1,1,1),(1,1,1),(1,1,1),(1,1,1)]
  Symmetry = 1
  TangentialDistance = 25
FEATURE [PartDesign::ShapeBinder] CopyRevolution004
  Placement = pos=(0,0,0) rot=(1,0,0;1.5708rad)
  TraceSupport = false
FEATURE [Sketcher::SketchObject] Sketch005
  ArcFitTolerance = 1e-06
  AttachmentSupport = -> [CopyRevolution004]
  FullyConstrained = true
  MakeInternals = false
  MapMode = 5
  Placement = pos=(0,2.11e-14,48) rot=(0,0,1;3.14159rad)
  sketch-geometry (1):
    g0: Circle CenterX=0 CenterY=0 CenterZ=0 NormalX=0 NormalY=0 NormalZ=1 AngleXU=0 Radius=140
  constraints (2):
    c: Coincident(g0,g-1)
    c: Radius(g0) = 140
FEATURE [PartDesign::Pad] Pad004
  Direction = (0,0,1)
  Length = 2
  Length2 = 10
  Placement = pos=(0,0,0) rot=(1,0,0;1.5708rad)
  Profile = -> Sketch005
  ReferenceAxis = -> Sketch005 [N_Axis]
  Refine = true
  Suppressed = false
  Type = 0
FEATURE [PartDesign::Body] Body005
  AllowCompound = false
  Group = -> [CopyRevolution004,Sketch005,Pad004]
  Origin = -> Origin005
  Tip = -> Pad004
FEATURE [App::Part] Part  label="clock1"
  Group = -> [Body,Body001,Body002,Body003,Array,Body005]
  Origin = -> Origin006
  Placement = pos=(0,0,0) rot=(1,0,0;1.5708rad)
FEATURE [App::Part] Part001  label="clock2"
  Group = -> [Part]
  Origin = -> Origin007
  Placement = pos=(0,0,150) rot=(0,0,1;0rad)
FEATURE [App::Part] Part002  label="clock3"
  Group = -> [Part001]
  Origin = -> Origin008
  Placement = pos=(0,0,150) rot=(0,0,1;0rad)
FEATURE [Part::FeaturePython] Clone  label="around"  # Draft clone (typed FeaturePython)
  AttacherType = Attacher::AttachEngine3D
  Fuse = false
  Objects = -> [Body]
  Placement = pos=(0,0,150) rot=(1,0,0;1.5708rad)
  Scale = (1,1,1)
FEATURE [App::Part] Part003  label="around_p"
  Group = -> [Clone]
  Origin = -> Origin009
  Placement = pos=(0,0,150) rot=(0,0,1;0rad)
FEATURE [Part::FeaturePython] Clone001  label="hour"  # Draft clone (typed FeaturePython)
  AttacherType = Attacher::AttachEngine3D
  Fuse = false
  Objects = -> [Body002]
  Placement = pos=(0,0,1) rot=(0,0,1;1.0472rad)
  Scale = (1,1,1)
FEATURE [App::Part] Part005  label="hour1"
  Group = -> [Clone001]
  Origin = -> Origin011
  Placement = pos=(0,0,150) rot=(1,0,0;1.5708rad)
FEATURE [App::Part] Part004  label="hour_p"
  Group = -> [Part005]
  Origin = -> Origin010
  Placement = pos=(0,0,150) rot=(0,0,1;0rad)
FEATURE [Part::FeaturePython] Clone002  label="minute"  # Draft clone (typed FeaturePython)
  AttacherType = Attacher::AttachEngine3D
  Fuse = false
  Objects = -> [Body001]
  Scale = (1,1,1)
FEATURE [App::Part] Part007  label="minute1"
  Group = -> [Clone002]
  Origin = -> Origin013
  Placement = pos=(0,0,150) rot=(1,0,0;1.5708rad)
FEATURE [App::Part] Part006  label="minute_p"
  Group = -> [Part007]
  Origin = -> Origin012
  Placement = pos=(0,0,150) rot=(0,0,1;0rad)
FEATURE [Part::FeaturePython] Clone003  label="symbol"  # Draft clone (typed FeaturePython)
  AttacherType = Attacher::AttachEngine3D
  Fuse = false
  Objects = -> [Array]
  Placement = pos=(0,0,150) rot=(1,0,0;1.5708rad)
  Scale = (1,1,1)
FEATURE [App::Part] Part008  label="symbol_p"
  Group = -> [Clone003]
  Origin = -> Origin014
  Placement = pos=(0,0,150) rot=(0,0,1;0rad)
FEATURE [Part::FeaturePython] Clone004  label="second"  # Draft clone (typed FeaturePython)
  AttacherType = Attacher::AttachEngine3D
  Fuse = false
  Objects = -> [Body003]
  Placement = pos=(0,0,2) rot=(0,0,1;0rad)
  Scale = (1,1,1)
FEATURE [App::Part] Part010  label="second1"
  Group = -> [Clone004]
  Origin = -> Origin016
  Placement = pos=(0,0,150) rot=(1,0,0;1.5708rad)
FEATURE [App::Part] Part009  label="second_p"
  Group = -> [Part010]
  Origin = -> Origin015
  Placement = pos=(0,0,150) rot=(0,0,1;0rad)
FEATURE [Part::FeaturePython] Clone005  label="glass"  # Draft clone (typed FeaturePython)
  AttacherType = Attacher::AttachEngine3D
  Fuse = false
  Objects = -> [Body005]
  Placement = pos=(0,0,150) rot=(1,0,0;1.5708rad)
  Scale = (1,1,1)
FEATURE [App::Part] Part011  label="glass_p"
  Group = -> [Clone005]
  Origin = -> Origin017
  Placement = pos=(0,0,150) rot=(0,0,1;0rad)
FEATURE [Part::FeaturePython] Clone006  label="around_clone"  # Draft clone (typed FeaturePython)
  AttacherType = Attacher::AttachEngine3D
  Fuse = false
  Objects = -> [Part003]
  Scale = (1,1,1)
FEATURE [Part::FeaturePython] Clone007  label="hour_clone"  # Draft clone (typed FeaturePython)
  AttacherType = Attacher::AttachEngine3D
  Fuse = false
  Objects = -> [Part004]
  Scale = (1,1,1)
FEATURE [Part::FeaturePython] Clone008  label="minute_clone"  # Draft clone (typed FeaturePython)
  AttacherType = Attacher::AttachEngine3D
  Fuse = false
  Objects = -> [Part006]
  Scale = (1,1,1)
FEATURE [Part::FeaturePython] Clone009  label="second_clone"  # Draft clone (typed FeaturePython)
  AttacherType = Attacher::AttachEngine3D
  Fuse = false
  Objects = -> [Part009]
  Scale = (1,1,1)
FEATURE [Part::FeaturePython] Clone010  label="symbol_clone"  # Draft clone (typed FeaturePython)
  AttacherType = Attacher::AttachEngine3D
  Fuse = false
  Objects = -> [Part008]
  Scale = (1,1,1)
FEATURE [Part::FeaturePython] Clone011  label="glass_clone"  # Draft clone (typed FeaturePython)
  AttacherType = Attacher::AttachEngine3D
  Fuse = false
  Objects = -> [Part011]
  Scale = (1,1,1)
FEATURE [App::Part] Part012  label="clock"
  Group = -> [Clone006,Clone007,Clone008,Clone009,Clone010,Clone011]
  Origin = -> Origin018
COMPONENT P2 — recipe-attached ("cocktail", a linked part whose construction recipe lives in a companion FreeCAD document of the same project; that document's serialized recipe follows).
Construction recipe (the companion document, serialized — sketch geometry with constraints, then the solid features built on it; lengths are millimeters unless a unit is written):

FCSTD DOCUMENT  (FreeCAD 1.0R39109 (Git))
Label: cocktail
License: All rights reserved
LicenseURL: https://en.wikipedia.org/wiki/All_rights_reserved
objects: Sketcher::SketchObject×4, PartDesign::Body×3, Part::FeaturePython×3, PartDesign::Revolution×2, PartDesign::Fillet×2, App::Part×2, PartDesign::AdditivePipe×1
note: 29 computed .brp shape members not serialized (recipe doc carries the construction recipe); baked Part::Feature solids carry a one-line shape summary decoded from their .brp

FEATURE [Sketcher::SketchObject] Sketch
  ArcFitTolerance = 1e-06
  AttachmentSupport = -> [XZ_Plane]
  FullyConstrained = true
  MakeInternals = false
  MapMode = 5
  Placement = pos=(0,0,0) rot=(1,0,0;1.5708rad)
  sketch-geometry (18):
    g0: LineSegment StartX=0 StartY=50 StartZ=0 EndX=0 EndY=0 EndZ=0
    g1: LineSegment StartX=0 StartY=0 StartZ=0 EndX=40 EndY=0 EndZ=0
    g2: LineSegment StartX=40 StartY=0 StartZ=0 EndX=40 EndY=1 EndZ=0
    g3: LineSegment StartX=40 StartY=1 StartZ=0 EndX=2.5 EndY=2.5 EndZ=0
    g4: LineSegment StartX=2.5 StartY=2.5 StartZ=0 EndX=2.5 EndY=47.5 EndZ=0
    g5: Circle [constr] CenterX=0 CenterY=50 CenterZ=0 NormalX=0 NormalY=0 NormalZ=1 AngleXU=0 Radius=1
    g6: Circle [constr] CenterX=40 CenterY=82.5 CenterZ=0 NormalX=0 NormalY=0 NormalZ=1 AngleXU=0 Radius=1
    g7: Circle [constr] CenterX=40 CenterY=150 CenterZ=0 NormalX=0 NormalY=0 NormalZ=1 AngleXU=0 Radius=1
    g8: BSplineCurve PolesCount=3 KnotsCount=2 Degree=2 IsPeriodic=0
    g9: GeomPoint [constr] X=0 Y=50 Z=0
    g10: GeomPoint [constr] X=40 Y=150 Z=0
    g11: Circle [constr] CenterX=42.5 CenterY=150 CenterZ=0 NormalX=0 NormalY=0 NormalZ=1 AngleXU=0 Radius=1
    g12: Circle [constr] CenterX=42.5 CenterY=80 CenterZ=0 NormalX=0 NormalY=0 NormalZ=1 AngleXU=0 Radius=1
    g13: Circle [constr] CenterX=2.5 CenterY=47.5 CenterZ=0 NormalX=0 NormalY=0 NormalZ=1 AngleXU=0 Radius=1
    g14: BSplineCurve PolesCount=3 KnotsCount=2 Degree=2 IsPeriodic=0
    g15: GeomPoint [constr] X=42.5 Y=150 Z=0
    g16: GeomPoint [constr] X=2.5 Y=47.5 Z=0
    g17: LineSegment StartX=40 StartY=150 StartZ=0 EndX=42.5 EndY=150 EndZ=0
  constraints (43):
    c: PointOnObject(g0,g-2)
    c: Coincident(g0,g-1)
    c: Coincident(g0,g1)
    c: PointOnObject(g1,g-1)
    c: Coincident(g1,g2)
    c: Vertical(g2)
    c: Coincident(g2,g3)
    c: Coincident(g3,g4)
    c: Vertical(g4)
    c: DistanceY(g0,g0) = 50
    c: DistanceX(g1) = 40
    c: DistanceY(g2) = 1
    c: DistanceY(g0,g3) = 2.5
    c: DistanceX(g0,g3) = 2.5
    c: DistanceY(g4,g0) = 2.5
    c: Weight(g5) = 1
    c: Equal(g5,g6)
    c: Equal(g5,g7)
    c: InternalAlignment(g5,g8)
    c: InternalAlignment(g6,g8)
    c: InternalAlignment(g7,g8)
    c: InternalAlignment(g9,g8)
    c: InternalAlignment(g10,g8)
    c: Coincident(g5,g0)
    c: Weight(g11) = 1
    c: Equal(g11,g12)
    c: Equal(g11,g13)
    c: InternalAlignment(g11,g14)
    c: InternalAlignment(g12,g14)
    c: InternalAlignment(g13,g14)
    c: InternalAlignment(g15,g14)
    c: InternalAlignment(g16,g14)
    c: Coincident(g13,g4)
    c: DistanceY(g12,g6) = 2.5
    c: DistanceY(g12) = 80
    c: Vertical(g14,g12)
    c: Vertical(g6,g8)
    c: DistanceY(g14) = 150
    c: DistanceX(g8) = 40
    c: Coincident(g17,g8)
    c: Coincident(g17,g14)
    c: Horizontal(g17)
    c: DistanceX(g17,g17) = 2.5
FEATURE [PartDesign::Revolution] Revolution
  Angle = 360
  Angle2 = 60
  Axis = (0,2e-16,1)
  Base = (0,0,0)
  Placement = pos=(0,0,0) rot=(1,0,0;1.5708rad)
  Profile = -> Sketch
  ReferenceAxis = -> Sketch [V_Axis]
  Refine = true
  Reversed = true
  Suppressed = false
  Type = 0
FEATURE [PartDesign::Fillet] Fillet
  Base = -> Revolution [Face6]
  BaseFeature = -> Revolution
  Placement = pos=(0,0,0) rot=(1,0,0;1.5708rad)
  Radius = 0.5
  Refine = true
  SupportTransform = false
  Suppressed = false
  UseAllEdges = false
FEATURE [PartDesign::Fillet] Fillet001
  Base = -> Fillet [Edge6,Edge3]
  BaseFeature = -> Fillet
  Placement = pos=(0,0,0) rot=(1,0,0;1.5708rad)
  Radius = 5
  Refine = true
  SupportTransform = false
  Suppressed = false
  UseAllEdges = false
FEATURE [PartDesign::Body] Body
  AllowCompound = false
  Group = -> [Sketch,Revolution,Fillet,Fillet001]
  Origin = -> Origin
  Tip = -> Fillet001
FEATURE [Sketcher::SketchObject] Sketch001
  ArcFitTolerance = 1e-06
  AttachmentSupport = -> [XZ_Plane001]
  FullyConstrained = true
  MakeInternals = false
  MapMode = 5
  Placement = pos=(0,0,0) rot=(1,0,0;1.5708rad)
  sketch-geometry (8):
    g0: LineSegment StartX=0 StartY=120 StartZ=0 EndX=0 EndY=50 EndZ=0
    g1: LineSegment StartX=0 StartY=120 StartZ=0 EndX=37.5 EndY=120 EndZ=0
    g2: Circle [constr] CenterX=37.5 CenterY=120 CenterZ=0 NormalX=0 NormalY=0 NormalZ=1 AngleXU=0 Radius=1
    g3: Circle [constr] CenterX=30 CenterY=75 CenterZ=0 NormalX=0 NormalY=0 NormalZ=1 AngleXU=0 Radius=1
    g4: Circle [constr] CenterX=0 CenterY=50 CenterZ=0 NormalX=0 NormalY=0 NormalZ=1 AngleXU=0 Radius=1
    g5: BSplineCurve PolesCount=3 KnotsCount=2 Degree=2 IsPeriodic=0
    g6: GeomPoint [constr] X=37.5 Y=120 Z=0
    g7: GeomPoint [constr] X=0 Y=50 Z=0
  constraints (19):
    c: Coincident(g0,g1)
    c: Horizontal(g1)
    c: Vertical(g0)
    c: PointOnObject(g0,g-2)
    c: DistanceY(g0) = 50
    c: DistanceX(g1) = 37.5
    c: Weight(g2) = 1
    c: Equal(g2,g3)
    c: Equal(g2,g4)
    c: InternalAlignment(g2,g5)
    c: InternalAlignment(g3,g5)
    c: InternalAlignment(g4,g5)
    c: InternalAlignment(g6,g5)
    c: InternalAlignment(g7,g5)
    c: Coincident(g4,g0)
    c: Coincident(g5,g1)
    c: DistanceX(g3) = 30
    c: DistanceY(g3) = 75
    c: DistanceY(g1) = 120
FEATURE [PartDesign::Revolution] Revolution001
  Angle = 360
  Angle2 = 60
  Axis = (0,2e-16,1)
  Base = (0,0,0)
  Placement = pos=(0,0,0) rot=(1,0,0;1.5708rad)
  Profile = -> Sketch001
  ReferenceAxis = -> Sketch001 [V_Axis]
  Refine = true
  Reversed = true
  Suppressed = false
  Type = 0
FEATURE [PartDesign::Body] Body001
  AllowCompound = false
  Group = -> [Sketch001,Revolution001]
  Origin = -> Origin001
  Tip = -> Revolution001
FEATURE [Sketcher::SketchObject] Sketch002
  ArcFitTolerance = 1e-06
  AttachmentSupport = -> [XZ_Plane002]
  FullyConstrained = true
  MakeInternals = false
  MapMode = 5
  Placement = pos=(0,0,0) rot=(1,0,0;1.5708rad)
  sketch-geometry (2):
    g0: LineSegment StartX=0 StartY=53 StartZ=0 EndX=45.6096 EndY=169.382 EndZ=0
    g1: LineSegment StartX=45.6096 StartY=169.382 StartZ=0 EndX=84.3394 EndY=179.382 EndZ=0
  constraints (7):
    c: PointOnObject(g0,g-2)
    c: Coincident(g0,g1)
    c: Distance(g1) = 40
    c: Distance(g0) = 125
    c: DistanceY(g0) = 53
    c: DistanceY(g0,g1) = 10
    c: Angle(g-1,g0) = 1.1973
FEATURE [Sketcher::SketchObject] Sketch003
  ArcFitTolerance = 1e-06
  AttachmentSupport = -> [XY_Plane002]
  FullyConstrained = true
  MakeInternals = false
  Placement = pos=(0,0,53) rot=(0,1,0;0.3735rad)
  sketch-geometry (2):
    g0: Circle CenterX=0 CenterY=0 CenterZ=0 NormalX=0 NormalY=0 NormalZ=1 AngleXU=0 Radius=1.8
    g1: Circle CenterX=0 CenterY=0 CenterZ=0 NormalX=0 NormalY=0 NormalZ=1 AngleXU=0 Radius=2
  constraints (4):
    c: Coincident(g0,g-1)
    c: Coincident(g1,g0)
    c: Radius(g1) = 2
    c: Radius(g0) = 1.8
FEATURE [PartDesign::AdditivePipe] AdditivePipe
  AuxilleryCurvelinear = true
  AuxillerySpineTangent = false
  Binormal = (0,0,0)
  Mode = 0
  Profile = -> Sketch003
  Refine = true
  Spine = -> Sketch002
  SpineTangent = false
  Suppressed = false
  Transformation = 0
  Transition = 2
FEATURE [PartDesign::Body] Body002
  AllowCompound = false
  Group = -> [Sketch002,Sketch003,AdditivePipe]
  Origin = -> Origin002
  Tip = -> AdditivePipe
FEATURE [App::Part] Part  label="cocktail_p"
  Group = -> [Body,Body001,Body002]
  Origin = -> Origin003
FEATURE [Part::FeaturePython] Clone  label="glass"  # Draft clone (typed FeaturePython)
  AttacherType = Attacher::AttachEngine3D
  Fuse = false
  Objects = -> [Body]
  Scale = (1,1,1)
FEATURE [Part::FeaturePython] Clone001  label="content"  # Draft clone (typed FeaturePython)
  AttacherType = Attacher::AttachEngine3D
  Fuse = false
  Objects = -> [Body001]
  Scale = (1,1,1)
FEATURE [Part::FeaturePython] Clone002  label="straw"  # Draft clone (typed FeaturePython)
  AttacherType = Attacher::AttachEngine3D
  Fuse = false
  Objects = -> [Body002]
  Scale = (1,1,1)
FEATURE [App::Part] Part001  label="cocktail"
  Group = -> [Clone,Clone001,Clone002]
  Origin = -> Origin004
COMPONENT P3 — same part as P2; its construction recipe is shown at P2.
COMPONENT P4 — same part as P2; its construction recipe is shown at P2.
COMPONENT P5 — geometry summary ("dressing_table"; no construction recipe available for this part):
  bounding box: 2399.9 x 1500.0 x 865.0 mm
  tessellated surface: 10,416 triangles
  volume: 896640949 mm^3 (29% of its bounding box)
  symmetry: mirror-symmetric across its y mid-plane
COMPONENT P6 — recipe-attached ("furniture", a linked part whose construction recipe lives in a companion FreeCAD document of the same project; that document's serialized recipe follows).
Construction recipe (the companion document, serialized — sketch geometry with constraints, then the solid features built on it; lengths are millimeters unless a unit is written):

FCSTD DOCUMENT  (FreeCAD 1.0R39109 (Git))
Label: furniture
License: All rights reserved
LicenseURL: https://en.wikipedia.org/wiki/All_rights_reserved
objects: App::Part×4, Sketcher::SketchObject×3, PartDesign::Pad×3, Part::FeaturePython×3, PartDesign::Body×2, Assembly::JointGroup×2, App::Link×2, Assembly::AssemblyObject×2, PartDesign::Fillet×1, PartDesign::Thickness×1, PartDesign::ShapeBinder×1, PartDesign::Plane×1
note: 27 computed .brp shape members not serialized (recipe doc carries the construction recipe); baked Part::Feature solids carry a one-line shape summary decoded from their .brp

FEATURE [Sketcher::SketchObject] Sketch
  ArcFitTolerance = 1e-06
  AttachmentSupport = -> [XY_Plane]
  FullyConstrained = true
  MakeInternals = false
  MapMode = 5
  sketch-geometry (4):
    g0: LineSegment StartX=-600 StartY=200 StartZ=0 EndX=-600 EndY=-200 EndZ=0
    g1: LineSegment StartX=-600 StartY=-200 StartZ=0 EndX=600 EndY=-200 EndZ=0
    g2: LineSegment StartX=600 StartY=-200 StartZ=0 EndX=600 EndY=200 EndZ=0
    g3: LineSegment StartX=600 StartY=200 StartZ=0 EndX=-600 EndY=200 EndZ=0
  constraints (11):
    c: Coincident(g0,g1)
    c: Coincident(g1,g2)
    c: Coincident(g2,g3)
    c: Coincident(g3,g0)
    c: Vertical(g0)
    c: Vertical(g2)
    c: Horizontal(g1)
    c: Horizontal(g3)
    c: Symmetric(g1,g0,g-1)
    c: DistanceX(g3,g3) = 1200
    c: DistanceY(g0,g0) = 400
FEATURE [PartDesign::Pad] Pad
  Direction = (0,0,1)
  Length = 600
  Length2 = 10
  Midplane = true
  Profile = -> Sketch
  ReferenceAxis = -> Sketch [N_Axis]
  Refine = true
  Suppressed = false
  Type = 0
FEATURE [PartDesign::Fillet] Fillet
  Base = -> Pad [Edge8,Edge5,Face5,Edge2,Edge1]
  BaseFeature = -> Pad
  Radius = 50
  Refine = true
  SupportTransform = false
  Suppressed = false
  UseAllEdges = false
FEATURE [PartDesign::Thickness] Thickness
  Base = -> Fillet [Face2]
  BaseFeature = -> Fillet
  Intersection = false
  Join = 0
  Mode = 0
  Refine = true
  Reversed = true
  SupportTransform = false
  Suppressed = false
  Value = 25
FEATURE [Sketcher::SketchObject] Sketch001
  ArcFitTolerance = 1e-06
  AttachmentSupport = -> [Thickness]
  ExternalGeometry = -> [Thickness]
  FullyConstrained = true
  MakeInternals = false
  MapMode = 5
  Placement = pos=(0,0,300) rot=(0,0,1;0rad)
  sketch-geometry (4):
    g0: LineSegment StartX=-575 StartY=12.5 StartZ=0 EndX=-575 EndY=-12.5 EndZ=0
    g1: LineSegment StartX=-575 StartY=-12.5 StartZ=0 EndX=575 EndY=-12.5 EndZ=0
    g2: LineSegment StartX=575 StartY=-12.5 StartZ=0 EndX=575 EndY=12.5 EndZ=0
    g3: LineSegment StartX=575 StartY=12.5 StartZ=0 EndX=-575 EndY=12.5 EndZ=0
  constraints (11):
    c: Coincident(g1,g2)
    c: Coincident(g2,g3)
    c: Coincident(g3,g0)
    c: Vertical(g0)
    c: Vertical(g2)
    c: Horizontal(g3)
    c: Coincident(g0,g1)
    c: PointOnObject(g0,g-4)
    c: Symmetric(g2,g0,g-1)
    c: Parallel(g1,g3)
    c: DistanceY(g0,g0) = 25
FEATURE [PartDesign::Pad] Pad001
  BaseFeature = -> Thickness
  Direction = (0,0,1)
  Length = 10
  Length2 = 10
  Profile = -> Sketch001
  ReferenceAxis = -> Sketch001 [N_Axis]
  Refine = true
  Suppressed = false
  Type = 3
  UpToFace = -> Thickness [Face28]
FEATURE [PartDesign::Body] Body
  AllowCompound = false
  Group = -> [Sketch,Pad,Fillet,Thickness,Sketch001,Pad001]
  Origin = -> Origin
  Tip = -> Pad001
FEATURE [PartDesign::ShapeBinder] CopyPad001
  TraceSupport = false
FEATURE [PartDesign::Plane] DatumPlane
  AttachmentSupport = -> [CopyPad001]
  Length = 60
  MapMode = 5
  Placement = pos=(0,0,300) rot=(0,0,1;0rad)
  ResizeMode = 0
  Width = 60
FEATURE [Sketcher::SketchObject] Sketch002
  ArcFitTolerance = 1e-06
  AttachmentSupport = -> [CopyPad001]
  ExternalGeometry = -> [CopyPad001]
  FullyConstrained = true
  MakeInternals = false
  MapMode = 5
  Placement = pos=(0,0,300) rot=(0,0,1;0rad)
  sketch-geometry (12):
    g0: ArcOfCircle CenterX=-550 CenterY=-150 CenterZ=0 NormalX=0 NormalY=0 NormalZ=1 AngleXU=0 Radius=74.9999 StartAngle=3.14159 EndAngle=4.71239
    g1: ArcOfCircle CenterX=550 CenterY=-150 CenterZ=0 NormalX=0 NormalY=0 NormalZ=1 AngleXU=0 Radius=50 StartAngle=4.71239 EndAngle=6.28319
    g2: ArcOfCircle CenterX=550 CenterY=-150 CenterZ=0 NormalX=0 NormalY=0 NormalZ=1 AngleXU=0 Radius=75 StartAngle=4.71239 EndAngle=6.28318
    g3: ArcOfCircle CenterX=-550 CenterY=-150 CenterZ=0 NormalX=0 NormalY=0 NormalZ=1 AngleXU=0 Radius=49.9999 StartAngle=3.14159 EndAngle=4.71239
    g4: LineSegment StartX=-550 StartY=-225 StartZ=0 EndX=550 EndY=-225 EndZ=0
    g5: LineSegment StartX=-625 StartY=-150 StartZ=0 EndX=-625 EndY=100 EndZ=0
    g6: LineSegment StartX=-625 StartY=100 StartZ=0 EndX=-600 EndY=100 EndZ=0
    g7: LineSegment StartX=-600 StartY=100 StartZ=0 EndX=-600 EndY=-150 EndZ=0
    g8: LineSegment StartX=625 StartY=-150 StartZ=0 EndX=625 EndY=100 EndZ=0
    g9: LineSegment StartX=625 StartY=100 StartZ=0 EndX=600 EndY=100 EndZ=0
    g10: LineSegment StartX=600 StartY=100 StartZ=0 EndX=600 EndY=-150 EndZ=0
    g11: LineSegment StartX=-550 StartY=-200 StartZ=0 EndX=550 EndY=-200 EndZ=0
  constraints (31):
    c: Coincident(g1,g-4)
    c: Coincident(g2,g1)
    c: Coincident(g3,g0)
    c: Coincident(g3,g-6)
    c: Coincident(g4,g0)
    c: Horizontal(g4)
    c: Vertical(g5)
    c: PointOnObject(g6,g-6)
    c: Horizontal(g6)
    c: Coincident(g7,g6)
    c: Coincident(g7,g3)
    c: Coincident(g8,g2)
    c: Vertical(g8)
    c: Coincident(g9,g8)
    c: PointOnObject(g9,g-3)
    c: Horizontal(g9)
    c: Coincident(g10,g9)
    c: Coincident(g1,g-4)
    c: Coincident(g11,g1)
    c: Horizontal(g11)
    c: DistanceX(g6,g6) = 25
    c: Coincident(g5,g6)
    c: Equal(g9,g6)
    c: DistanceY(g6,g-6) = 50
    c: Equal(g5,g8)
    c: Tangent(g0,g4,g0) = -1.5708
    c: Tangent(g4,g2) = -1.5708
    c: Tangent(g10,g1) = 1.5708
    c: DistanceY(g9,g-3) = 50
    c: Tangent(g5,g0) = 1.5708
    c: Tangent(g11,g3) = -1.5708
FEATURE [PartDesign::Pad] Pad002
  Direction = (0,0,1)
  Length = 50
  Length2 = 10
  Midplane = true
  Profile = -> Sketch002
  ReferenceAxis = -> Sketch002 [N_Axis]
  Refine = true
  Suppressed = false
  Type = 0
FEATURE [PartDesign::Body] Body001
  AllowCompound = false
  Group = -> [DatumPlane,CopyPad001,Sketch002,Pad002]
  Origin = -> Origin001
  Placement = pos=(0,0,-150) rot=(0,0,1;0rad)
  Tip = -> Pad002
FEATURE [Part::FeaturePython] Array  # Draft array (typed FeaturePython)
  AlwaysSyncPlacement = false
  Angle = 360
  ArrayType = 0
  Axis = (0,0,1)
  Base = -> Body001
  Center = (0,0,0)
  Count = 2
  ExpandArray = false
  Fuse = false
  IntervalAxis = (0,0,0)
  IntervalX = (100,0,0)
  IntervalY = (0,100,0)
  IntervalZ = (0,0,-350)
  NumberCircles = 3
  NumberPolar = 5
  NumberX = 1
  NumberY = 1
  NumberZ = 2
  PlacementList = 2 placements: [(0,0,-150),(0,0,-500)]
  RadialDistance = 50
  ScaleList = (2) [(1,1,1),(1,1,1)]
  Symmetry = 1
  TangentialDistance = 25
FEATURE [App::Part] Part  label="furniture1"
  Group = -> [Body,Array]
  Origin = -> Origin002
  Placement = pos=(0,0,0) rot=(1,0,0;1.5708rad)
FEATURE [App::Part] Part001  label="furniture2"
  Group = -> [Part]
  Origin = -> Origin003
  Placement = pos=(0,0,225) rot=(0,0,1;0rad)
FEATURE [App::Part] Part002  label="furniture3"
  Group = -> [Part001]
  Origin = -> Origin004
  Placement = pos=(0,0,225) rot=(0,0,1;0rad)
FEATURE [Assembly::JointGroup] Joints
FEATURE [Assembly::JointGroup] Joints001
FEATURE [App::Link] Body002
  LinkPlacement = pos=(0,0,225) rot=(1,0,0;1.5708rad)
  LinkedObject = -> Body
  Placement = pos=(0,0,225) rot=(1,0,0;1.5708rad)
FEATURE [Assembly::AssemblyObject] Assembly  label="body_a"
  Group = -> [Joints,Body002]
  Origin = -> Origin005
  Placement = pos=(0,0,225) rot=(0,0,1;0rad)
  Type = Assembly
FEATURE [App::Link] Array001
  LinkPlacement = pos=(0,0,225) rot=(1,0,0;1.5708rad)
  LinkedObject = -> Array
  Placement = pos=(0,0,225) rot=(1,0,0;1.5708rad)
FEATURE [Assembly::AssemblyObject] Assembly001  label="stand_a"
  Group = -> [Joints001,Array001]
  Origin = -> Origin006
  Placement = pos=(0,0,225) rot=(0,0,1;0rad)
  Type = Assembly
FEATURE [Part::FeaturePython] Clone  label="body_clone"  # Draft clone (typed FeaturePython)
  AttacherType = Attacher::AttachEngine3D
  Fuse = false
  Objects = -> [Assembly]
  Scale = (1,1,1)
FEATURE [Part::FeaturePython] Clone001  label="stand_clone"  # Draft clone (typed FeaturePython)
  AttacherType = Attacher::AttachEngine3D
  Fuse = false
  Objects = -> [Assembly001]
  Scale = (1,1,1)
FEATURE [App::Part] Part003  label="furniture"
  Group = -> [Clone,Clone001]
  Origin = -> Origin007
COMPONENT P7 — recipe-attached ("moniter", a linked part whose construction recipe lives in a companion FreeCAD document of the same project; that document's serialized recipe follows).
Construction recipe (the companion document, serialized — sketch geometry with constraints, then the solid features built on it; lengths are millimeters unless a unit is written):

FCSTD DOCUMENT  (FreeCAD 1.0R39109 (Git))
Label: moniter
License: All rights reserved
LicenseURL: https://en.wikipedia.org/wiki/All_rights_reserved
objects: Sketcher::SketchObject×8, PartDesign::Pad×6, PartDesign::Body×3, PartDesign::Fillet×2, PartDesign::Pocket×2, PartDesign::ShapeBinder×2, Part::FeaturePython×2, Part::Fuse×1, App::Part×1
note: 54 computed .brp shape members not serialized (recipe doc carries the construction recipe); baked Part::Feature solids carry a one-line shape summary decoded from their .brp

FEATURE [Sketcher::SketchObject] Sketch
  ArcFitTolerance = 1e-06
  AttachmentSupport = -> [XY_Plane]
  FullyConstrained = false
  MakeInternals = false
  MapMode = 5
  sketch-geometry (17):
    g0: LineSegment StartX=-47.8454 StartY=29.1131 StartZ=0 EndX=47.8454 EndY=29.1131 EndZ=0
    g1: LineSegment StartX=61.011 StartY=51.3954 StartZ=0 EndX=40.1625 EndY=89.247 EndZ=0
    g2: LineSegment StartX=17.5666 StartY=102.598 StartZ=0 EndX=-17.5666 EndY=102.598 EndZ=0
    g3: LineSegment StartX=-40.1625 StartY=89.247 StartZ=0 EndX=-61.011 EndY=51.3954 EndZ=0
    g4: GeomPoint [constr] X=0 Y=0 Z=0
    g5: ArcOfCircle CenterX=-17.5666 CenterY=76.8013 CenterZ=0 NormalX=0 NormalY=0 NormalZ=1 AngleXU=0 Radius=25.7967 StartAngle=1.5708 EndAngle=2.63814
    g6: GeomPoint [constr] X=-32.8089 Y=102.598 Z=0
    g7: ArcOfCircle CenterX=17.5666 CenterY=76.8013 CenterZ=0 NormalX=0 NormalY=0 NormalZ=1 AngleXU=0 Radius=25.7967 StartAngle=0.503453 EndAngle=1.5708
    g8: GeomPoint [constr] X=32.8089 Y=102.598 Z=0
    g9: ArcOfCircle CenterX=47.8454 CenterY=44.1438 CenterZ=0 NormalX=0 NormalY=0 NormalZ=1 AngleXU=0 Radius=15.0306 StartAngle=4.71239 EndAngle=6.78664
    g10: GeomPoint [constr] X=73.284 Y=29.1131 Z=0
    g11: ArcOfCircle CenterX=-47.8454 CenterY=44.1438 CenterZ=0 NormalX=0 NormalY=0 NormalZ=1 AngleXU=0 Radius=15.0306 StartAngle=2.63814 EndAngle=4.71239
    g12: GeomPoint [constr] X=-73.284 Y=29.1131 Z=0
    g13: LineSegment [constr] StartX=-17.5666 StartY=76.8013 StartZ=0 EndX=47.8454 EndY=44.1438 EndZ=0
    g14: LineSegment [constr] StartX=17.5666 StartY=76.8013 StartZ=0 EndX=-47.8454 EndY=44.1438 EndZ=0
    g15: LineSegment [constr] StartX=17.5666 StartY=76.8013 StartZ=0 EndX=47.8454 EndY=44.1438 EndZ=0
    g16: LineSegment [constr] StartX=-17.5666 StartY=76.8013 StartZ=0 EndX=-47.8454 EndY=44.1438 EndZ=0
  constraints (30):
    c: Horizontal(g0)
    c: Horizontal(g2)
    c: Coincident(g4,g-1)
    c: PointOnObject(g6,g2)
    c: PointOnObject(g6,g3)
    c: Tangent(g2,g5) = -1.5708
    c: Tangent(g3,g5) = -1.5708
    c: PointOnObject(g8,g2)
    c: PointOnObject(g8,g1)
    c: Tangent(g2,g7) = -1.5708
    c: Tangent(g1,g7) = -1.5708
    c: PointOnObject(g10,g1)
    c: PointOnObject(g10,g0)
    c: Tangent(g1,g9) = -1.5708
    c: Tangent(g0,g9) = -1.5708
    c: PointOnObject(g12,g3)
    c: PointOnObject(g12,g0)
    c: Tangent(g3,g11) = -1.5708
    c: Tangent(g0,g11) = -1.5708
    c: Equal(g11,g9)
    c: Coincident(g13,g5)
    c: Coincident(g13,g9)
    c: Coincident(g14,g7)
    c: Coincident(g14,g11)
    c: Equal(g14,g13)
    c: Symmetric(g7,g5,g-2)
    c: Coincident(g15,g7)
    c: Coincident(g15,g9)
    c: Coincident(g16,g5)
    c: Coincident(g16,g11)
FEATURE [PartDesign::Pad] Pad
  Direction = (0,0,1)
  Length = 10
  Length2 = 10
  Profile = -> Sketch
  ReferenceAxis = -> Sketch [N_Axis]
  Refine = true
  Suppressed = false
  Type = 0
FEATURE [Sketcher::SketchObject] Sketch001
  ArcFitTolerance = 1e-06
  AttachmentSupport = -> [Pad]
  FullyConstrained = false
  MakeInternals = false
  MapMode = 5
  Placement = pos=(0,0,10) rot=(0,0,1;0rad)
  sketch-geometry (10):
    g0: LineSegment StartX=-30.568 StartY=79.6606 StartZ=0 EndX=-30.568 EndY=73.3721 EndZ=0
    g1: LineSegment StartX=-20.568 StartY=63.3721 StartZ=0 EndX=20.568 EndY=63.3721 EndZ=0
    g2: LineSegment StartX=30.568 StartY=73.3721 StartZ=0 EndX=30.568 EndY=79.6619 EndZ=0
    g3: ArcOfCircle CenterX=0.00125496 CenterY=43.2656 CenterZ=0 NormalX=0 NormalY=0 NormalZ=1 AngleXU=0 Radius=52.8585 StartAngle=1.09908 EndAngle=2.04258
    g4: ArcOfCircle CenterX=-18.568 CenterY=79.6606 CenterZ=0 NormalX=0 NormalY=0 NormalZ=1 AngleXU=0 Radius=12 StartAngle=2.04258 EndAngle=3.14159
    g5: ArcOfCircle CenterX=18.568 CenterY=79.6619 CenterZ=0 NormalX=0 NormalY=0 NormalZ=1 AngleXU=0 Radius=12 StartAngle=1e-16 EndAngle=1.09908
    g6: ArcOfCircle CenterX=20.568 CenterY=73.3721 CenterZ=0 NormalX=0 NormalY=0 NormalZ=1 AngleXU=0 Radius=10 StartAngle=4.71239 EndAngle=6.28319
    g7: GeomPoint [constr] X=30.568 Y=63.3721 Z=0
    g8: ArcOfCircle CenterX=-20.568 CenterY=73.3721 CenterZ=0 NormalX=0 NormalY=0 NormalZ=1 AngleXU=0 Radius=10 StartAngle=3.14159 EndAngle=4.71239
    g9: GeomPoint [constr] X=-30.568 Y=63.3721 Z=0
  constraints (19):
    c: Vertical(g0)
    c: Vertical(g2)
    c: Symmetric(g9,g7,g-2)
    c: Tangent(g3,g4) = -1.5708
    c: Tangent(g0,g4) = -1.5708
    c: Tangent(g3,g5) = -1.5708
    c: Tangent(g2,g5) = -1.5708
    c: PointOnObject(g7,g2)
    c: PointOnObject(g7,g1)
    c: Tangent(g2,g6) = -1.5708
    c: Tangent(g1,g6) = -1.5708
    c: PointOnObject(g9,g0)
    c: PointOnObject(g9,g1)
    c: Tangent(g0,g8) = -1.5708
    c: Tangent(g1,g8) = -1.5708
    c: Equal(g8,g6)
    c: Equal(g5,g4)
    c: Radius(g8) = 10
    c: Radius(g4) = 12
FEATURE [Sketcher::SketchObject] Sketch002
  ArcFitTolerance = 1e-06
  AttachmentSupport = -> [XZ_Plane001]
  FullyConstrained = false
  MakeInternals = false
  MapMode = 5
  Placement = pos=(0,0,0) rot=(1,0,0;1.5708rad)
  sketch-geometry (4):
    g0: LineSegment StartX=-265.2 StartY=359.744 StartZ=0 EndX=-265.2 EndY=59.7441 EndZ=0
    g1: LineSegment StartX=-265.2 StartY=59.7441 StartZ=0 EndX=265.2 EndY=59.7441 EndZ=0
    g2: LineSegment StartX=265.2 StartY=59.7441 StartZ=0 EndX=265.2 EndY=359.744 EndZ=0
    g3: LineSegment StartX=265.2 StartY=359.744 StartZ=0 EndX=-265.2 EndY=359.744 EndZ=0
  constraints (10):
    c: Coincident(g0,g1)
    c: Coincident(g1,g2)
    c: Coincident(g2,g3)
    c: Coincident(g3,g0)
    c: Vertical(g0)
    c: Vertical(g2)
    c: Horizontal(g1)
    c: Distance(g0,g2) = 530.4
    c: Distance(g1,g3) = 300
    c: Symmetric(g2,g0,g-2)
FEATURE [PartDesign::Pad] Pad002
  Direction = (0,-1,2e-16)
  Length = 30
  Length2 = 10
  Placement = pos=(0,0,0) rot=(1,0,0;1.5708rad)
  Profile = -> Sketch002
  ReferenceAxis = -> Sketch002 [N_Axis]
  Refine = true
  Reversed = true
  Suppressed = false
  TaperAngle = -20
  Type = 0
FEATURE [PartDesign::Fillet] Fillet
  Base = -> Pad002 [Edge6,Edge9,Edge4,Edge2]
  BaseFeature = -> Pad002
  Placement = pos=(0,0,0) rot=(1,0,0;1.5708rad)
  Radius = 5
  Refine = true
  SupportTransform = false
  Suppressed = false
  UseAllEdges = false
FEATURE [Sketcher::SketchObject] Sketch003
  ArcFitTolerance = 1e-06
  AttachmentSupport = -> [Fillet]
  FullyConstrained = false
  MakeInternals = false
  MapMode = 5
  Placement = pos=(0,30,-1.38e-14) rot=(-1,0,0;1.5708rad)
  sketch-geometry (4):
    g0: LineSegment StartX=190.861 StartY=-107.821 StartZ=0 EndX=190.861 EndY=-55.3481 EndZ=0
    g1: LineSegment StartX=190.861 StartY=-55.3481 StartZ=0 EndX=-190.861 EndY=-55.3481 EndZ=0
    g2: LineSegment StartX=-190.861 StartY=-55.3481 StartZ=0 EndX=-190.861 EndY=-107.821 EndZ=0
    g3: LineSegment StartX=-190.861 StartY=-107.821 StartZ=0 EndX=190.861 EndY=-107.821 EndZ=0
  constraints (8):
    c: Coincident(g0,g1)
    c: Coincident(g1,g2)
    c: Coincident(g2,g3)
    c: Coincident(g3,g0)
    c: Vertical(g0)
    c: Vertical(g2)
    c: Horizontal(g1)
    c: Symmetric(g2,g0,g-2)
FEATURE [PartDesign::Pocket] Pocket
  BaseFeature = -> Fillet
  Direction = (0,-1,-2e-16)
  Length = 20
  Length2 = 5
  Placement = pos=(0,0,0) rot=(1,0,0;1.5708rad)
  Profile = -> Sketch003
  ReferenceAxis = -> Sketch003 [N_Axis]
  Refine = true
  Suppressed = false
  Type = 0
FEATURE [Sketcher::SketchObject] Sketch004
  ArcFitTolerance = 1e-06
  AttachmentSupport = -> [Pocket]
  FullyConstrained = false
  MakeInternals = false
  MapMode = 5
  Placement = pos=(0,30,-1.38e-14) rot=(-1,0,0;1.5708rad)
  sketch-geometry (14):
    g0: LineSegment StartX=60 StartY=-228.06 StartZ=0 EndX=60 EndY=-128.06 EndZ=0
    g1: LineSegment StartX=50 StartY=-118.06 StartZ=0 EndX=-50 EndY=-118.06 EndZ=0
    g2: LineSegment StartX=-60 StartY=-128.06 StartZ=0 EndX=-60 EndY=-228.06 EndZ=0
    g3: LineSegment StartX=-50 StartY=-238.06 StartZ=0 EndX=50 EndY=-238.06 EndZ=0
    g4: ArcOfCircle CenterX=50 CenterY=-228.06 CenterZ=0 NormalX=0 NormalY=0 NormalZ=1 AngleXU=0 Radius=10 StartAngle=4.71239 EndAngle=6.28319
    g5: ArcOfCircle CenterX=50 CenterY=-128.06 CenterZ=0 NormalX=0 NormalY=0 NormalZ=1 AngleXU=0 Radius=10 StartAngle=1.1e-15 EndAngle=1.5708
    g6: ArcOfCircle CenterX=-50 CenterY=-128.06 CenterZ=0 NormalX=0 NormalY=0 NormalZ=1 AngleXU=0 Radius=10 StartAngle=1.5708 EndAngle=3.14159
    g7: ArcOfCircle CenterX=-50 CenterY=-228.06 CenterZ=0 NormalX=0 NormalY=0 NormalZ=1 AngleXU=0 Radius=10 StartAngle=3.14159 EndAngle=4.71239
    g8: GeomPoint [constr] X=60 Y=-238.06 Z=0
    g9: GeomPoint [constr] X=-60 Y=-118.06 Z=0
    g10: Circle CenterX=50 CenterY=-228.06 CenterZ=0 NormalX=0 NormalY=0 NormalZ=1 AngleXU=0 Radius=2
    g11: Circle CenterX=-50 CenterY=-228.06 CenterZ=0 NormalX=0 NormalY=0 NormalZ=1 AngleXU=0 Radius=2
    g12: Circle CenterX=50 CenterY=-128.06 CenterZ=0 NormalX=0 NormalY=0 NormalZ=1 AngleXU=0 Radius=2
    g13: Circle CenterX=-50 CenterY=-128.06 CenterZ=0 NormalX=0 NormalY=0 NormalZ=1 AngleXU=0 Radius=2
  constraints (30):
    c: Tangent(g0,g4) = -1.5708
    c: Tangent(g0,g5) = -1.5708
    c: Tangent(g1,g5) = -1.5708
    c: Tangent(g1,g6) = -1.5708
    c: Tangent(g2,g6) = -1.5708
    c: Tangent(g2,g7) = -1.5708
    c: Tangent(g3,g7) = -1.5708
    c: Tangent(g3,g4) = -1.5708
    c: Vertical(g0)
    c: Vertical(g2)
    c: Horizontal(g1)
    c: Horizontal(g3)
    c: Equal(g4,g5)
    c: Equal(g5,g6)
    c: PointOnObject(g8,g0)
    c: PointOnObject(g8,g3)
    c: PointOnObject(g9,g1)
    c: PointOnObject(g9,g2)
    c: DistanceX(g7,g4) = 100
    c: DistanceY(g7,g6) = 100
    c: Symmetric(g4,g7,g-2)
    c: Radius(g4) = 10
    c: Coincident(g10,g4)
    c: Coincident(g11,g7)
    c: Coincident(g12,g5)
    c: Coincident(g13,g6)
    c: Equal(g13,g11)
    c: Equal(g11,g10)
    c: Equal(g10,g12)
    c: Radius(g10) = 2
FEATURE [PartDesign::Pad] Pad003
  BaseFeature = -> Pocket
  Direction = (0,1,2e-16)
  Length = 2
  Length2 = 10
  Placement = pos=(0,0,0) rot=(1,0,0;1.5708rad)
  Profile = -> Sketch004
  ReferenceAxis = -> Sketch004 [N_Axis]
  Refine = true
  Suppressed = false
  Type = 0
FEATURE [PartDesign::Pad] Pad001
  BaseFeature = -> Pad
  Direction = (0,0,1)
  Length = 204
  Length2 = 10
  Profile = -> Sketch001
  ReferenceAxis = -> Sketch001 [N_Axis]
  Refine = true
  Suppressed = false
  Type = 0
FEATURE [PartDesign::ShapeBinder] CopyPad003
  Placement = pos=(0,2,4e-16) rot=(0,0,1;0rad)
  TraceSupport = false
FEATURE [Sketcher::SketchObject] Sketch005
  ArcFitTolerance = 1e-06
  AttachmentSupport = -> [CopyPad003]
  ExternalGeometry = -> [CopyPad003]
  FullyConstrained = false
  MakeInternals = false
  MapMode = 5
  Placement = pos=(0,32,7.3e-15) rot=(0,0.707107,0.707107;3.14159rad)
  sketch-geometry (12):
    g0: LineSegment [constr] StartX=-60 StartY=228.06 StartZ=0 EndX=60 EndY=128.06 EndZ=0
    g1: LineSegment [constr] StartX=60 StartY=228.06 StartZ=0 EndX=-7.1e-15 EndY=178.06 EndZ=0
    g2: LineSegment StartX=-17.106 StartY=184.304 StartZ=0 EndX=-17.106 EndY=171.815 EndZ=0
    g3: LineSegment StartX=-12.1108 StartY=166.82 StartZ=0 EndX=12.1108 EndY=166.82 EndZ=0
    g4: LineSegment StartX=17.106 StartY=171.815 StartZ=0 EndX=17.106 EndY=184.304 EndZ=0
    g5: LineSegment StartX=12.1108 StartY=189.299 StartZ=0 EndX=-12.1108 EndY=189.299 EndZ=0
    g6: ArcOfCircle CenterX=-12.1108 CenterY=184.304 CenterZ=0 NormalX=0 NormalY=0 NormalZ=1 AngleXU=0 Radius=4.99514 StartAngle=1.5708 EndAngle=3.14159
    g7: ArcOfCircle CenterX=-12.1108 CenterY=171.815 CenterZ=0 NormalX=0 NormalY=0 NormalZ=1 AngleXU=0 Radius=4.99514 StartAngle=3.14159 EndAngle=4.71239
    g8: ArcOfCircle CenterX=12.1108 CenterY=171.815 CenterZ=0 NormalX=0 NormalY=0 NormalZ=1 AngleXU=0 Radius=4.99514 StartAngle=4.71239 EndAngle=6.28319
    g9: ArcOfCircle CenterX=12.1108 CenterY=184.304 CenterZ=0 NormalX=0 NormalY=0 NormalZ=1 AngleXU=0 Radius=4.99514 StartAngle=8e-16 EndAngle=1.5708
    g10: GeomPoint [constr] X=-17.106 Y=189.299 Z=0
    g11: GeomPoint [constr] X=17.106 Y=166.82 Z=0
  constraints (23):
    c: Coincident(g0,g-4)
    c: Coincident(g0,g-5)
    c: Coincident(g1,g-4)
    c: Symmetric(g0,g0,g1)
    c: Tangent(g2,g6) = -1.5708
    c: Tangent(g2,g7) = -1.5708
    c: Tangent(g3,g7) = -1.5708
    c: Tangent(g3,g8) = -1.5708
    c: Tangent(g4,g8) = -1.5708
    c: Tangent(g4,g9) = -1.5708
    c: Tangent(g5,g9) = -1.5708
    c: Tangent(g5,g6) = -1.5708
    c: Vertical(g2)
    c: Vertical(g4)
    c: Horizontal(g3)
    c: Horizontal(g5)
    c: Equal(g7,g8)
    c: PointOnObject(g10,g2)
    c: PointOnObject(g10,g5)
    c: PointOnObject(g11,g3)
    c: PointOnObject(g11,g4)
    c: Symmetric(g9,g6,g-2)
    c: Symmetric(g9,g7,g1)
FEATURE [PartDesign::Pad] Pad004
  BaseFeature = -> Pad001
  Direction = (0,1,-2e-16)
  Length = 10
  Length2 = 10
  Profile = -> Sketch005
  ReferenceAxis = -> Sketch005 [N_Axis]
  Refine = true
  Suppressed = false
  Type = 3
  UpToFace = -> Pad001 [Face13]
FEATURE [PartDesign::Fillet] Fillet001
  Base = -> Pad004 [Edge10]
  BaseFeature = -> Pad004
  Radius = 2
  Refine = true
  SupportTransform = false
  Suppressed = false
  UseAllEdges = false
FEATURE [PartDesign::Body] Body
  AllowCompound = false
  Group = -> [Sketch,Pad,Sketch001,Pad001,CopyPad003,Sketch005,Pad004,Fillet001]
  Origin = -> Origin
  Tip = -> Fillet001
FEATURE [Sketcher::SketchObject] Sketch006
  ArcFitTolerance = 1e-06
  AttachmentSupport = -> [Pad003]
  ExternalGeometry = -> [Pad003]
  FullyConstrained = true
  MakeInternals = false
  MapMode = 5
  Placement = pos=(0,1.5e-15,0) rot=(1,0,0;1.5708rad)
  sketch-geometry (9):
    g0: LineSegment StartX=260.502 StartY=64.4426 StartZ=0 EndX=260.502 EndY=355.046 EndZ=0
    g1: LineSegment StartX=260.502 StartY=355.046 StartZ=0 EndX=-260.502 EndY=355.046 EndZ=0
    g2: LineSegment StartX=-260.502 StartY=355.046 StartZ=0 EndX=-260.502 EndY=64.4426 EndZ=0
    g3: LineSegment StartX=-260.502 StartY=64.4426 StartZ=0 EndX=260.502 EndY=64.4426 EndZ=0
    g4: GeomPoint [constr] X=0 Y=209.744 Z=0
    g5: LineSegment [constr] StartX=-260.502 StartY=359.744 StartZ=0 EndX=-260.502 EndY=355.046 EndZ=0
    g6: LineSegment [constr] StartX=260.502 StartY=64.4426 StartZ=0 EndX=260.502 EndY=59.7441 EndZ=0
    g7: LineSegment [constr] StartX=265.2 StartY=64.4426 StartZ=0 EndX=260.502 EndY=64.4426 EndZ=0
    g8: LineSegment [constr] StartX=-265.2 StartY=355.046 StartZ=0 EndX=-260.502 EndY=355.046 EndZ=0
  constraints (21):
    c: Coincident(g0,g1)
    c: Coincident(g1,g2)
    c: Coincident(g2,g3)
    c: Coincident(g3,g0)
    c: Vertical(g0)
    c: Vertical(g2)
    c: Horizontal(g1)
    c: Horizontal(g3)
    c: Symmetric(g2,g0,g4)
    c: PointOnObject(g4,g-2)
    c: Coincident(g5,g-3)
    c: Coincident(g5,g1)
    c: Coincident(g6,g0)
    c: Coincident(g6,g-6)
    c: Vertical(g6)
    c: Equal(g5,g6)
    c: Coincident(g7,g-4)
    c: Coincident(g7,g0)
    c: Coincident(g8,g-5)
    c: Coincident(g8,g1)
    c: Equal(g8,g5)
FEATURE [PartDesign::Pocket] Pocket001
  BaseFeature = -> Pad003
  Direction = (0,1,-2e-16)
  Length = 5
  Length2 = 5
  Placement = pos=(0,0,0) rot=(1,0,0;1.5708rad)
  Profile = -> Sketch006
  ReferenceAxis = -> Sketch006 [N_Axis]
  Refine = true
  Suppressed = false
  Type = 0
FEATURE [PartDesign::Body] Body001
  AllowCompound = false
  Group = -> [Sketch002,Pad002,Fillet,Sketch003,Pocket,Sketch004,Pad003,Sketch006,Pocket001]
  Origin = -> Origin001
  Tip = -> Pocket001
FEATURE [Part::Fuse] Fusion  label="moniter_body"
  Base = -> Body
  Refine = true
  Tool = -> Body001
FEATURE [PartDesign::ShapeBinder] CopyPocket001
  Placement = pos=(0,5,-2e-15) rot=(0,0,1;0rad)
  TraceSupport = false
FEATURE [Sketcher::SketchObject] Sketch007
  ArcFitTolerance = 1e-06
  AttachmentSupport = -> [CopyPocket001]
  ExternalGeometry = -> [CopyPocket001]
  FullyConstrained = true
  MakeInternals = false
  MapMode = 5
  Placement = pos=(0,5,-2e-15) rot=(1,0,0;1.5708rad)
  sketch-geometry (4):
    g0: LineSegment StartX=-260.502 StartY=355.046 StartZ=0 EndX=-260.502 EndY=64.4426 EndZ=0
    g1: LineSegment StartX=-260.502 StartY=64.4426 StartZ=0 EndX=260.502 EndY=64.4426 EndZ=0
    g2: LineSegment StartX=260.502 StartY=64.4426 StartZ=0 EndX=260.502 EndY=355.046 EndZ=0
    g3: LineSegment StartX=260.502 StartY=355.046 StartZ=0 EndX=-260.502 EndY=355.046 EndZ=0
  constraints (10):
    c: Coincident(g0,g1)
    c: Coincident(g1,g2)
    c: Coincident(g2,g3)
    c: Coincident(g3,g0)
    c: Vertical(g0)
    c: Vertical(g2)
    c: Horizontal(g1)
    c: Horizontal(g3)
    c: Coincident(g0,g-3)
    c: Coincident(g1,g-4)
FEATURE [PartDesign::Pad] Pad005
  Direction = (0,-1,2e-16)
  Length = 1
  Length2 = 10
  Placement = pos=(0,5,-2e-15) rot=(0,0,1;0rad)
  Profile = -> Sketch007
  ReferenceAxis = -> Sketch007 [N_Axis]
  Refine = true
  Suppressed = false
  Type = 0
FEATURE [PartDesign::Body] Body002  label="moniter_screen"
  AllowCompound = false
  Group = -> [CopyPocket001,Sketch007,Pad005]
  Origin = -> Origin002
  Tip = -> Pad005
FEATURE [Part::FeaturePython] Clone  label="moniter_body_clone"  # Draft clone (typed FeaturePython)
  AttacherType = Attacher::AttachEngine3D
  Fuse = false
  Objects = -> [Fusion]
  Scale = (1,1,1)
FEATURE [Part::FeaturePython] Clone001  label="moniter_screen_clone"  # Draft clone (typed FeaturePython)
  AttacherType = Attacher::AttachEngine3D
  Fuse = false
  Objects = -> [Body002]
  Scale = (1,1,1)
FEATURE [App::Part] Part  label="moniter"
  Group = -> [Clone,Clone001]
  Origin = -> Origin004
COMPONENT P8 — same part as P7; its construction recipe is shown at P7.
COMPONENT P9 — recipe-attached ("pylon", a linked part whose construction recipe lives in a companion FreeCAD document of the same project; that document's serialized recipe follows).
Construction recipe (the companion document, serialized — sketch geometry with constraints, then the solid features built on it; lengths are millimeters unless a unit is written):

FCSTD DOCUMENT  (FreeCAD 1.0R39109 (Git))
Label: pylon
License: All rights reserved
LicenseURL: https://en.wikipedia.org/wiki/All_rights_reserved
objects: Sketcher::SketchObject×2, App::Part×2, PartDesign::Pad×1, PartDesign::Revolution×1, PartDesign::Fillet×1, PartDesign::Thickness×1, PartDesign::Body×1, Part::FeaturePython×1
note: 18 computed .brp shape members not serialized (recipe doc carries the construction recipe); baked Part::Feature solids carry a one-line shape summary decoded from their .brp

FEATURE [Sketcher::SketchObject] Sketch
  ArcFitTolerance = 1e-06
  AttachmentSupport = -> [XY_Plane]
  FullyConstrained = true
  MakeInternals = false
  MapMode = 5
  sketch-geometry (4):
    g0: LineSegment StartX=-125 StartY=125 StartZ=0 EndX=-125 EndY=-125 EndZ=0
    g1: LineSegment StartX=-125 StartY=-125 StartZ=0 EndX=125 EndY=-125 EndZ=0
    g2: LineSegment StartX=125 StartY=-125 StartZ=0 EndX=125 EndY=125 EndZ=0
    g3: LineSegment StartX=125 StartY=125 StartZ=0 EndX=-125 EndY=125 EndZ=0
  constraints (11):
    c: Coincident(g0,g1)
    c: Coincident(g1,g2)
    c: Coincident(g2,g3)
    c: Coincident(g3,g0)
    c: Vertical(g0)
    c: Vertical(g2)
    c: Horizontal(g1)
    c: Horizontal(g3)
    c: Symmetric(g0,g1,g-1)
    c: DistanceX(g3,g3) = 250
    c: Equal(g3,g0)
FEATURE [PartDesign::Pad] Pad
  Direction = (0,0,1)
  Length = 10
  Length2 = 10
  Profile = -> Sketch
  ReferenceAxis = -> Sketch [N_Axis]
  Refine = true
  Reversed = true
  Suppressed = false
  Type = 0
FEATURE [Sketcher::SketchObject] Sketch001
  ArcFitTolerance = 1e-06
  AttachmentSupport = -> [XZ_Plane]
  FullyConstrained = true
  MakeInternals = false
  MapMode = 5
  Placement = pos=(0,0,0) rot=(1,0,0;1.5708rad)
  sketch-geometry (13):
    g0: LineSegment StartX=115 StartY=0 StartZ=0 EndX=0 EndY=0 EndZ=0
    g1: LineSegment StartX=0 StartY=0 StartZ=0 EndX=0 EndY=500 EndZ=0
    g2: LineSegment StartX=0 StartY=500 StartZ=0 EndX=20 EndY=500 EndZ=0
    g3: LineSegment StartX=20 StartY=500 StartZ=0 EndX=33 EndY=405 EndZ=0
    g4: LineSegment StartX=33 StartY=405 StartZ=0 EndX=32.9009 EndY=404.986 EndZ=0
    g5: LineSegment StartX=32.9009 StartY=404.986 StartZ=0 EndX=45.9009 EndY=309.986 EndZ=0
    g6: LineSegment StartX=45.9009 StartY=309.986 StartZ=0 EndX=46 EndY=310 EndZ=0
    g7: LineSegment StartX=46 StartY=310 StartZ=0 EndX=59 EndY=215 EndZ=0
    g8: LineSegment StartX=59 StartY=215 StartZ=0 EndX=58.9009 EndY=214.986 EndZ=0
    g9: LineSegment StartX=58.9009 StartY=214.986 StartZ=0 EndX=71.9009 EndY=119.986 EndZ=0
    g10: LineSegment StartX=71.9009 StartY=119.986 StartZ=0 EndX=72 EndY=120 EndZ=0
    g11: LineSegment StartX=72 StartY=120 StartZ=0 EndX=85 EndY=25 EndZ=0
    g12: LineSegment StartX=85 StartY=25 StartZ=0 EndX=115 EndY=0 EndZ=0
  constraints (38):
    c: PointOnObject(g0,g-1)
    c: Coincident(g0,g-1)
    c: Coincident(g0,g1)
    c: Vertical(g1)
    c: Coincident(g1,g2)
    c: Coincident(g2,g3)
    c: Coincident(g3,g4)
    c: Coincident(g4,g5)
    c: Coincident(g5,g6)
    c: Coincident(g6,g7)
    c: Coincident(g7,g8)
    c: Coincident(g8,g9)
    c: Coincident(g9,g10)
    c: Coincident(g10,g11)
    c: Equal(g3,g5)
    c: Equal(g5,g7)
    c: Equal(g7,g9)
    c: Perpendicular(g4,g3)
    c: Perpendicular(g7,g6)
    c: Perpendicular(g6,g5)
    c: Perpendicular(g5,g4)
    c: Perpendicular(g9,g8)
    c: Perpendicular(g8,g7)
    c: Perpendicular(g9,g10)
    c: Perpendicular(g10,g11)
    c: Horizontal(g2)
    c: Equal(g4,g6)
    c: Equal(g6,g8)
    c: Equal(g8,g10)
    c: DistanceX(g0,g0) = 115
    c: DistanceY(g1,g1) = 500
    c: Distance(g6) = 0.1
    c: DistanceX(g2,g2) = 20
    c: Coincident(g12,g11)
    c: Coincident(g12,g0)
    c: DistanceY(g11) = 25
    c: DistanceX(g12,g12) = 30
    c: Equal(g9,g11)
FEATURE [PartDesign::Revolution] Revolution
  Angle = 360
  Angle2 = 60
  Axis = (0,2e-16,1)
  Base = (0,0,0)
  BaseFeature = -> Pad
  Profile = -> Sketch001
  ReferenceAxis = -> Sketch001 [V_Axis]
  Refine = true
  Reversed = true
  Suppressed = false
  Type = 0
FEATURE [PartDesign::Fillet] Fillet
  Base = -> Revolution [Edge26,Edge29,Edge31,Edge27]
  BaseFeature = -> Revolution
  Radius = 25
  Refine = true
  SupportTransform = false
  Suppressed = false
  UseAllEdges = false
FEATURE [PartDesign::Thickness] Thickness
  Base = -> Fillet [Face11,Face21]
  BaseFeature = -> Fillet
  Intersection = false
  Join = 1
  Mode = 0
  Refine = true
  Reversed = true
  SupportTransform = false
  Suppressed = false
  Value = 3
FEATURE [PartDesign::Body] Body
  AllowCompound = false
  Group = -> [Sketch,Pad,Sketch001,Revolution,Fillet,Thickness]
  Origin = -> Origin
  Placement = pos=(0,0,10) rot=(0,0,1;0rad)
  Tip = -> Thickness
FEATURE [App::Part] Part
  Group = -> [Body]
  Origin = -> Origin001
  Placement = pos=(0,0,10) rot=(0,0,1;0rad)
FEATURE [Part::FeaturePython] Clone  label="pylon_clone"  # Draft clone (typed FeaturePython)
  AttacherType = Attacher::AttachEngine3D
  Fuse = false
  Objects = -> [Part]
  Scale = (1,1,1)
FEATURE [App::Part] Part001  label="pylon"
  Group = -> [Clone]
  Origin = -> Origin002
COMPONENT P10 — same part as P9; its construction recipe is shown at P9.
COMPONENT P11 — same part as P9; its construction recipe is shown at P9.
COMPONENT P12 — recipe-attached ("refrigerator", a linked part whose construction recipe lives in a companion FreeCAD document of the same project; that document's serialized recipe follows).
Construction recipe (the companion document, serialized — sketch geometry with constraints, then the solid features built on it; lengths are millimeters unless a unit is written):

FCSTD DOCUMENT  (FreeCAD 1.0R39109 (Git))
Label: refrigerator
License: All rights reserved
LicenseURL: https://en.wikipedia.org/wiki/All_rights_reserved
objects: Sketcher::SketchObject×4, PartDesign::Pad×4, PartDesign::Body×1, Part::FeaturePython×1, App::Part×1
note: 22 computed .brp shape members not serialized (recipe doc carries the construction recipe); baked Part::Feature solids carry a one-line shape summary decoded from their .brp

FEATURE [Sketcher::SketchObject] Sketch
  ArcFitTolerance = 1e-06
  AttachmentSupport = -> [XY_Plane]
  FullyConstrained = true
  MakeInternals = false
  MapMode = 5
  sketch-geometry (5):
    g0: LineSegment StartX=-370 StartY=-364.5 StartZ=0 EndX=370 EndY=-364.5 EndZ=0
    g1: LineSegment StartX=370 StartY=-364.5 StartZ=0 EndX=370 EndY=364.5 EndZ=0
    g2: LineSegment StartX=370 StartY=364.5 StartZ=0 EndX=-370 EndY=364.5 EndZ=0
    g3: LineSegment StartX=-370 StartY=364.5 StartZ=0 EndX=-370 EndY=-364.5 EndZ=0
    g4: GeomPoint [constr] X=0 Y=0 Z=0
  constraints (12):
    c: Coincident(g0,g1)
    c: Coincident(g1,g2)
    c: Coincident(g2,g3)
    c: Coincident(g3,g0)
    c: Horizontal(g0)
    c: Horizontal(g2)
    c: Vertical(g1)
    c: Vertical(g3)
    c: Symmetric(g2,g0,g4)
    c: Distance(g1,g3) = 740
    c: Distance(g0,g2) = 729
    c: Coincident(g4,g-1)
FEATURE [PartDesign::Pad] Pad
  Direction = (0,0,1)
  Length = 1818
  Length2 = 10
  Profile = -> Sketch
  ReferenceAxis = -> Sketch [N_Axis]
  Refine = true
  Suppressed = false
  Type = 0
FEATURE [Sketcher::SketchObject] Sketch001
  ArcFitTolerance = 1e-06
  AttachmentSupport = -> [Pad]
  ExternalGeometry = -> [Pad]
  FullyConstrained = true
  MakeInternals = false
  MapMode = 5
  Placement = pos=(0,-364.5,0) rot=(1,0,0;1.5708rad)
  sketch-geometry (10):
    g0: LineSegment [constr] StartX=370 StartY=1818 StartZ=0 EndX=370 EndY=1813 EndZ=0
    g1: LineSegment [constr] StartX=370 StartY=1818 StartZ=0 EndX=365 EndY=1818 EndZ=0
    g2: LineSegment [constr] StartX=-370 StartY=0 StartZ=0 EndX=-370 EndY=5 EndZ=0
    g3: LineSegment [constr] StartX=-370 StartY=0 StartZ=0 EndX=-365 EndY=0 EndZ=0
    g4: LineSegment [constr] StartX=-370 StartY=5 StartZ=0 EndX=-365 EndY=5 EndZ=0
    g5: LineSegment [constr] StartX=370 StartY=1813 StartZ=0 EndX=365 EndY=1813 EndZ=0
    g6: LineSegment StartX=365 StartY=1813 StartZ=0 EndX=-365 EndY=1813 EndZ=0
    g7: LineSegment StartX=-365 StartY=1813 StartZ=0 EndX=-365 EndY=5 EndZ=0
    g8: LineSegment StartX=-365 StartY=5 StartZ=0 EndX=365 EndY=5 EndZ=0
    g9: LineSegment StartX=365 StartY=5 StartZ=0 EndX=365 EndY=1813 EndZ=0
  constraints (28):
    c: Distance(g0) = 5
    c: Coincident(g0,g-4)
    c: PointOnObject(g0,g-3)
    c: Distance(g1) = 5
    c: Coincident(g1,g0)
    c: PointOnObject(g1,g-4)
    c: Distance(g2) = 5
    c: Coincident(g2,g-5)
    c: PointOnObject(g2,g-5)
    c: Distance(g3) = 5
    c: Coincident(g3,g2)
    c: PointOnObject(g3,g-1)
    c: Distance(g4) = 5
    c: Coincident(g4,g2)
    c: Horizontal(g4)
    c: Distance(g5) = 5
    c: Coincident(g5,g0)
    c: Horizontal(g5)
    c: Coincident(g6,g7)
    c: Coincident(g7,g8)
    c: Coincident(g8,g9)
    c: Coincident(g9,g6)
    c: Horizontal(g6)
    c: Horizontal(g8)
    c: Vertical(g7)
    c: Vertical(g9)
    c: Coincident(g6,g5)
    c: Coincident(g7,g4)
FEATURE [PartDesign::Pad] Pad001
  BaseFeature = -> Pad
  Direction = (0,-1,2e-16)
  Length = 1
  Length2 = 10
  Profile = -> Sketch001
  ReferenceAxis = -> Sketch001 [N_Axis]
  Refine = true
  Suppressed = false
  Type = 0
FEATURE [Sketcher::SketchObject] Sketch002
  ArcFitTolerance = 1e-06
  AttachmentSupport = -> [Pad001]
  ExternalGeometry = -> [Pad001]
  FullyConstrained = false
  MakeInternals = false
  MapMode = 5
  Placement = pos=(0,-365.5,0) rot=(1,0,0;1.5708rad)
  sketch-geometry (8):
    g0: LineSegment StartX=-370 StartY=1818 StartZ=0 EndX=-370 EndY=909 EndZ=0
    g1: LineSegment StartX=370 StartY=909 StartZ=0 EndX=370 EndY=1818 EndZ=0
    g2: LineSegment StartX=370 StartY=1818 StartZ=0 EndX=-65.0129 EndY=1818 EndZ=0
    g3: LineSegment StartX=-70.0129 StartY=1818 StartZ=0 EndX=-70.0129 EndY=909 EndZ=0
    g4: LineSegment StartX=-65.0129 StartY=1818 StartZ=0 EndX=-65.0129 EndY=909 EndZ=0
    g5: LineSegment StartX=-70.0129 StartY=1818 StartZ=0 EndX=-370 EndY=1818 EndZ=0
    g6: LineSegment StartX=-70.0129 StartY=909 StartZ=0 EndX=-370 EndY=909 EndZ=0
    g7: LineSegment StartX=-65.0129 StartY=909 StartZ=0 EndX=370 EndY=909 EndZ=0
  constraints (17):
    c: Coincident(g1,g2)
    c: Coincident(g5,g0)
    c: Vertical(g0)
    c: Vertical(g1)
    c: Horizontal(g2)
    c: Coincident(g0,g-4)
    c: Vertical(g3)
    c: PointOnObject(g3,g5)
    c: Vertical(g4)
    c: Coincident(g2,g4)
    c: PointOnObject(g5,g3)
    c: Coincident(g6,g3)
    c: Coincident(g6,g0)
    c: Horizontal(g6)
    c: Coincident(g7,g4)
    c: Coincident(g7,g1)
    c: Horizontal(g7)
FEATURE [PartDesign::Pad] Pad002
  BaseFeature = -> Pad001
  Direction = (0,-1,2e-16)
  Length = 20
  Length2 = 10
  Profile = -> Sketch002
  ReferenceAxis = -> Sketch002 [N_Axis]
  Refine = true
  Suppressed = false
  Type = 0
FEATURE [Sketcher::SketchObject] Sketch003
  ArcFitTolerance = 1e-06
  AttachmentSupport = -> [Pad002]
  ExternalGeometry = -> [Pad002]
  FullyConstrained = false
  MakeInternals = false
  MapMode = 5
  Placement = pos=(0,-385.5,0) rot=(1,0,0;1.5708rad)
  sketch-geometry (19):
    g0: LineSegment StartX=-370 StartY=904.002 StartZ=0 EndX=-70 EndY=904.002 EndZ=0
    g1: LineSegment StartX=-65 StartY=904.002 StartZ=0 EndX=370 EndY=904.002 EndZ=0
    g2: LineSegment [constr] StartX=-70 StartY=904.002 StartZ=0 EndX=-65 EndY=904.002 EndZ=0
    g3: LineSegment StartX=-70 StartY=904.002 StartZ=0 EndX=-70 EndY=759.002 EndZ=0
    g4: LineSegment StartX=-70 StartY=759.002 StartZ=0 EndX=-370 EndY=759.002 EndZ=0
    g5: LineSegment StartX=-370 StartY=904.002 StartZ=0 EndX=-370 EndY=759.002 EndZ=0
    g6: LineSegment StartX=-65 StartY=904.002 StartZ=0 EndX=-65 EndY=759.002 EndZ=0
    g7: LineSegment StartX=370 StartY=904.002 StartZ=0 EndX=370 EndY=759.002 EndZ=0
    g8: LineSegment StartX=370 StartY=759.002 StartZ=0 EndX=-65 EndY=759.002 EndZ=0
    g9: LineSegment [constr] StartX=-370 StartY=759.002 StartZ=0 EndX=-370 EndY=754.002 EndZ=0
    g10: LineSegment StartX=-370 StartY=754.002 StartZ=0 EndX=-370 EndY=379.002 EndZ=0
    g11: LineSegment StartX=-370 StartY=379.002 StartZ=0 EndX=370 EndY=379.002 EndZ=0
    g12: LineSegment StartX=370 StartY=379.002 StartZ=0 EndX=370 EndY=754.002 EndZ=0
    g13: LineSegment StartX=370 StartY=754.002 StartZ=0 EndX=-370 EndY=754.002 EndZ=0
    g14: LineSegment [constr] StartX=-370 StartY=379.002 StartZ=0 EndX=-370 EndY=374.002 EndZ=0
    g15: LineSegment StartX=-370 StartY=374.002 StartZ=0 EndX=-370 EndY=0 EndZ=0
    g16: LineSegment StartX=-370 StartY=0 StartZ=0 EndX=370 EndY=0 EndZ=0
    g17: LineSegment StartX=370 StartY=0 StartZ=0 EndX=370 EndY=374.002 EndZ=0
    g18: LineSegment StartX=370 StartY=374.002 StartZ=0 EndX=-370 EndY=374.002 EndZ=0
  constraints (50):
    c: Horizontal(g0)
    c: Horizontal(g1)
    c: Distance(g2) = 5
    c: Coincident(g2,g0)
    c: Coincident(g2,g1)
    c: Horizontal(g2)
    c: DistanceX(g0,g0) = 300
    c: Distance(g3) = 145
    c: Coincident(g3,g0)
    c: Vertical(g3)
    c: Coincident(g4,g3)
    c: Horizontal(g4)
    c: Vertical(g5)
    c: Coincident(g4,g5)
    c: Distance(g6) = 145
    c: Coincident(g6,g1)
    c: Vertical(g6)
    c: Distance(g7) = 145
    c: Coincident(g7,g1)
    c: Vertical(g7)
    c: Coincident(g8,g7)
    c: Coincident(g8,g6)
    c: Distance(g9) = 5
    c: Coincident(g9,g4)
    c: Vertical(g9)
    c: Coincident(g10,g11)
    c: Coincident(g11,g12)
    c: Coincident(g12,g13)
    c: Coincident(g13,g10)
    c: Vertical(g10)
    c: Vertical(g12)
    c: Horizontal(g11)
    c: Horizontal(g13)
    c: Distance(g10,g12) = 740
    c: Distance(g11,g13) = 375
    c: Coincident(g10,g9)
    c: Coincident(g5,g0)
    c: Distance(g14) = 5
    c: Coincident(g14,g10)
    c: Vertical(g14)
    c: Coincident(g15,g16)
    c: Coincident(g16,g17)
    c: Coincident(g17,g18)
    c: Coincident(g18,g15)
    c: Vertical(g15)
    c: Vertical(g17)
    c: Horizontal(g16)
    c: Horizontal(g18)
    c: Coincident(g15,g14)
    c: Coincident(g16,g-7)
FEATURE [PartDesign::Pad] Pad003
  BaseFeature = -> Pad002
  Direction = (0,-1,2e-16)
  Length = 20
  Length2 = 10
  Profile = -> Sketch003
  ReferenceAxis = -> Sketch003 [N_Axis]
  Refine = true
  Reversed = true
  Suppressed = false
  Type = 0
FEATURE [PartDesign::Body] Body
  AllowCompound = false
  Group = -> [Sketch,Pad,Sketch001,Pad001,Sketch002,Pad002,Sketch003,Pad003]
  Origin = -> Origin
  Tip = -> Pad003
FEATURE [Part::FeaturePython] Clone  label="refrigerator_clone"  # Draft clone (typed FeaturePython)
  AttacherType = Attacher::AttachEngine3D
  Fuse = false
  Objects = -> [Body]
  Scale = (1,1,1)
FEATURE [App::Part] Part  label="refrigerator"
  Group = -> [Clone]
  Origin = -> Origin001
COMPONENT P13 — recipe-attached ("room", a linked part whose construction recipe lives in a companion FreeCAD document of the same project; that document's serialized recipe follows).
Construction recipe (the companion document, serialized — sketch geometry with constraints, then the solid features built on it; lengths are millimeters unless a unit is written):

FCSTD DOCUMENT  (FreeCAD 1.0R39109 (Git))
Label: room
License: All rights reserved
LicenseURL: https://en.wikipedia.org/wiki/All_rights_reserved
objects: Sketcher::SketchObject×3, Part::FeaturePython×3, App::GeometryPython×2, App::Part×1
note: 11 computed .brp shape members not serialized (recipe doc carries the construction recipe); baked Part::Feature solids carry a one-line shape summary decoded from their .brp

FEATURE [Sketcher::SketchObject] Sketch
  ArcFitTolerance = 1e-06
  FullyConstrained = true
  MakeInternals = false
  sketch-geometry (5):
    g0: LineSegment StartX=-2600 StartY=-2600 StartZ=0 EndX=2600 EndY=-2600 EndZ=0
    g1: LineSegment StartX=2600 StartY=-2600 StartZ=0 EndX=2600 EndY=2600 EndZ=0
    g2: LineSegment StartX=2600 StartY=2600 StartZ=0 EndX=-2600 EndY=2600 EndZ=0
    g3: LineSegment StartX=-2600 StartY=2600 StartZ=0 EndX=-2600 EndY=-2600 EndZ=0
    g4: GeomPoint [constr] X=1.53e-14 Y=4.1e-15 Z=0
  constraints (12):
    c: Coincident(g0,g1)
    c: Coincident(g1,g2)
    c: Coincident(g2,g3)
    c: Coincident(g3,g0)
    c: Horizontal(g0)
    c: Horizontal(g2)
    c: Vertical(g1)
    c: Vertical(g3)
    c: Symmetric(g2,g0,g4)
    c: Coincident(g4,g-1)
    c: DistanceX(g2,g2) = 5200
    c: Equal(g2,g3)
FEATURE [Part::FeaturePython] Structure  label="Slab"  # Arch/BIM 118 (typed FeaturePython)
  Base = -> Sketch
  BaseMirror = false
  BaseOffsetX = 0
  BaseOffsetY = 0
  BasePerpendicularToTool = false
  BaseRotation = 0
  ComputedLength = 200
  FaceMaker = 0
  Height = 200
  HorizontalArea = 27040000
  IfcData = attributes={"GlobalId": {"name": "GlobalId", "type": "IfcGloballyUniqueId", "is_enum": false, "enum_values": []}, "Description": {"... (+453 chars omitted),+1 more (map truncated)
  IfcType = 118
  Length = 0
  MoveBase = false
  MoveWithHost = false
  Nodes = (4) [(-2600,-2600,0),(2600,-2600,0),(2600,2600,0),(-2600,2600,0)]
  NodesOffset = 0
  Normal = (0,0,-1)
  PerimeterLength = 20800
  PredefinedType = 0
  ToolOffsetFirst = 0
  ToolOffsetLast = 0
  VerticalArea = 4160000
  Width = 100
FEATURE [Sketcher::SketchObject] Sketch001
  ArcFitTolerance = 1e-06
  FullyConstrained = true
  MakeInternals = false
  sketch-geometry (5):
    g0: LineSegment StartX=-2500 StartY=2500 StartZ=0 EndX=-2500 EndY=-2500 EndZ=0
    g1: LineSegment StartX=-2500 StartY=-2500 StartZ=0 EndX=2500 EndY=-2500 EndZ=0
    g2: LineSegment StartX=2500 StartY=-2500 StartZ=0 EndX=2500 EndY=2500 EndZ=0
    g3: LineSegment StartX=2500 StartY=2500 StartZ=0 EndX=-2500 EndY=2500 EndZ=0
    g4: GeomPoint [constr] X=-7.4e-15 Y=-2.5e-15 Z=0
  constraints (12):
    c: Coincident(g0,g1)
    c: Coincident(g1,g2)
    c: Coincident(g2,g3)
    c: Coincident(g3,g0)
    c: Vertical(g0)
    c: Vertical(g2)
    c: Horizontal(g1)
    c: Horizontal(g3)
    c: Symmetric(g2,g0,g4)
    c: Coincident(g4,g-1)
    c: DistanceX(g3,g3) = 5000
    c: Equal(g3,g0)
FEATURE [Part::FeaturePython] Wall  label="壁"  # Arch/BIM 166 (typed FeaturePython)
  Align = 2
  ArchSketchData = true
  Area = 60000000
  Base = -> Sketch001
  BlockHeight = 0
  BlockLength = 0
  CountBroken = 0
  CountEntire = 0
  Face = 0
  Height = 3000
  HorizontalArea = 2000000
  IfcData = attributes={"GlobalId": {"name": "GlobalId", "type": "IfcGloballyUniqueId", "is_enum": false, "enum_values": []}, "Description": {"... (+533 chars omitted),+1 more (map truncated)
  IfcType = 166
  Joint = 0
  Length = 20000
  MakeBlocks = false
  MoveBase = false
  MoveWithHost = false
  Normal = (0,0,0)
  OffsetFirst = 0
  OffsetSecond = 0
  PerimeterLength = 40000
  PredefinedType = 0
  VerticalArea = 116640000
  Width = 100
FEATURE [App::GeometryPython] BuildingPart001  label="Level"  # Arch/BIM 14 (typed FeaturePython)
  Area = 0
  CompositionType = 0
  Elevation = 0
  Group = -> [Sketch,Structure,Wall]
  Height = 0
  HeightPropagate = true
  IfcData = attributes={"GlobalId": {"name": "GlobalId", "type": "IfcGloballyUniqueId", "is_enum": false, "enum_values": []}, "Description": {"... (+845 chars omitted),+1 more (map truncated)
  IfcType = 14
  LevelOffset = 0
  LongName = Level
  MaterialsTable = Undefined=0,1,2,3
  OnlySolids = true
  expr: Elevation = .Placement.Base.z
FEATURE [App::GeometryPython] BuildingPart  label="ビルディング"  # Arch/BIM 10 (typed FeaturePython)
  Area = 0
  BuildingType = 0
  CompositionType = 0
  ElevationOfRefHeight = 0
  ElevationOfTerrain = 0
  Group = -> [BuildingPart001]
  Height = 0
  HeightPropagate = true
  IfcData = attributes={"GlobalId": {"name": "GlobalId", "type": "IfcGloballyUniqueId", "is_enum": false, "enum_values": []}, "Description": {"... (+1017 chars omitted),+1 more (map truncated)
  IfcType = 10
  LevelOffset = 0
  LongName = ビルディング
  MaterialsTable = Undefined=0,1,2,3
  OnlySolids = true
FEATURE [Sketcher::SketchObject] Sketch002
  ArcFitTolerance = 1e-06
  FullyConstrained = true
  MakeInternals = false
  Placement = pos=(1841,-2453,0) rot=(0,0.707107,0.707107;3.14159rad)
  sketch-geometry (8):
    g0: LineSegment StartX=0 StartY=0 StartZ=0 EndX=900 EndY=0 EndZ=0
    g1: LineSegment StartX=900 StartY=0 StartZ=0 EndX=900 EndY=2100 EndZ=0
    g2: LineSegment StartX=900 StartY=2100 StartZ=0 EndX=0 EndY=2100 EndZ=0
    g3: LineSegment StartX=0 StartY=2100 StartZ=0 EndX=0 EndY=0 EndZ=0
    g4: LineSegment StartX=49 StartY=0 StartZ=0 EndX=851 EndY=0 EndZ=0
    g5: LineSegment StartX=851 StartY=0 StartZ=0 EndX=851 EndY=2051 EndZ=0
    g6: LineSegment StartX=851 StartY=2051 StartZ=0 EndX=49 EndY=2051 EndZ=0
    g7: LineSegment StartX=49 StartY=2051 StartZ=0 EndX=49 EndY=0 EndZ=0
  constraints (23):
    c: Coincident(g0,g1)
    c: Coincident(g1,g2)
    c: Coincident(g2,g3)
    c: Coincident(g3,g0)
    c: Horizontal(g0)
    c: Horizontal(g2)
    c: Vertical(g1)
    c: Vertical(g3)
    c: Coincident(g4,g5)
    c: Coincident(g5,g6)
    c: Coincident(g6,g7)
    c: Coincident(g7,g4)
    c: Horizontal(g4)
    c: Horizontal(g6)
    c: Vertical(g5)
    c: Vertical(g7)
    c: DistanceY(g1) = 2100  'Height'
    c: DistanceX(g0) = 900  'Width'
    c: DistanceY(g6,g2) = 49  'Frame1'
    c: DistanceX(g2,g6) = 49  'Frame2'
    c: DistanceX(g4,g0) = 49  'Frame3'
    c: DistanceY(g0,g4) = 0
    c: Coincident(g0,g-1)
FEATURE [Part::FeaturePython] Window  label="Door"  # Arch/BIM 41 (typed FeaturePython)
  Area = 1890000
  Base = -> Sketch002
  Frame = 50
  Height = 2100
  HoleDepth = 0
  HoleWire = 0
  HorizontalArea = 0
  Hosts = -> [Wall]
  IfcData = attributes={"GlobalId": {"name": "GlobalId", "type": "IfcGloballyUniqueId", "is_enum": false, "enum_values": []}, "Description": {"... (+1933 chars omitted),+1 more (map truncated)
  IfcType = 41
  LouvreSpacing = 0
  LouvreWidth = 0
  MoveBase = false
  MoveWithHost = true
  Normal = (0,-1,2e-16)
  Offset = 50
  Opening = 40
  OperationType = 0
  OverallHeight = 2100
  OverallWidth = 900
  PerimeterLength = 0
  PredefinedType = 0
  Preset = 6
  SymbolElevation = false
  SymbolPlan = false
  VerticalArea = 0
  Width = 900
  WindowParts = OuterFrame | Frame | Wire0,Wire1 | 50.0+V | 0.00+V | Door | Solid panel | Wire1,Edge8,Mode1 | 50.0 | 50.0+V
  expr: OverallHeight = .Height.Value
  expr: OverallWidth = .Width.Value
FEATURE [App::Part] Part  label="room"
  Group = -> [BuildingPart001,Sketch001,Sketch,Sketch002,Structure,Wall,Window,BuildingPart]
  Origin = -> Origin001
